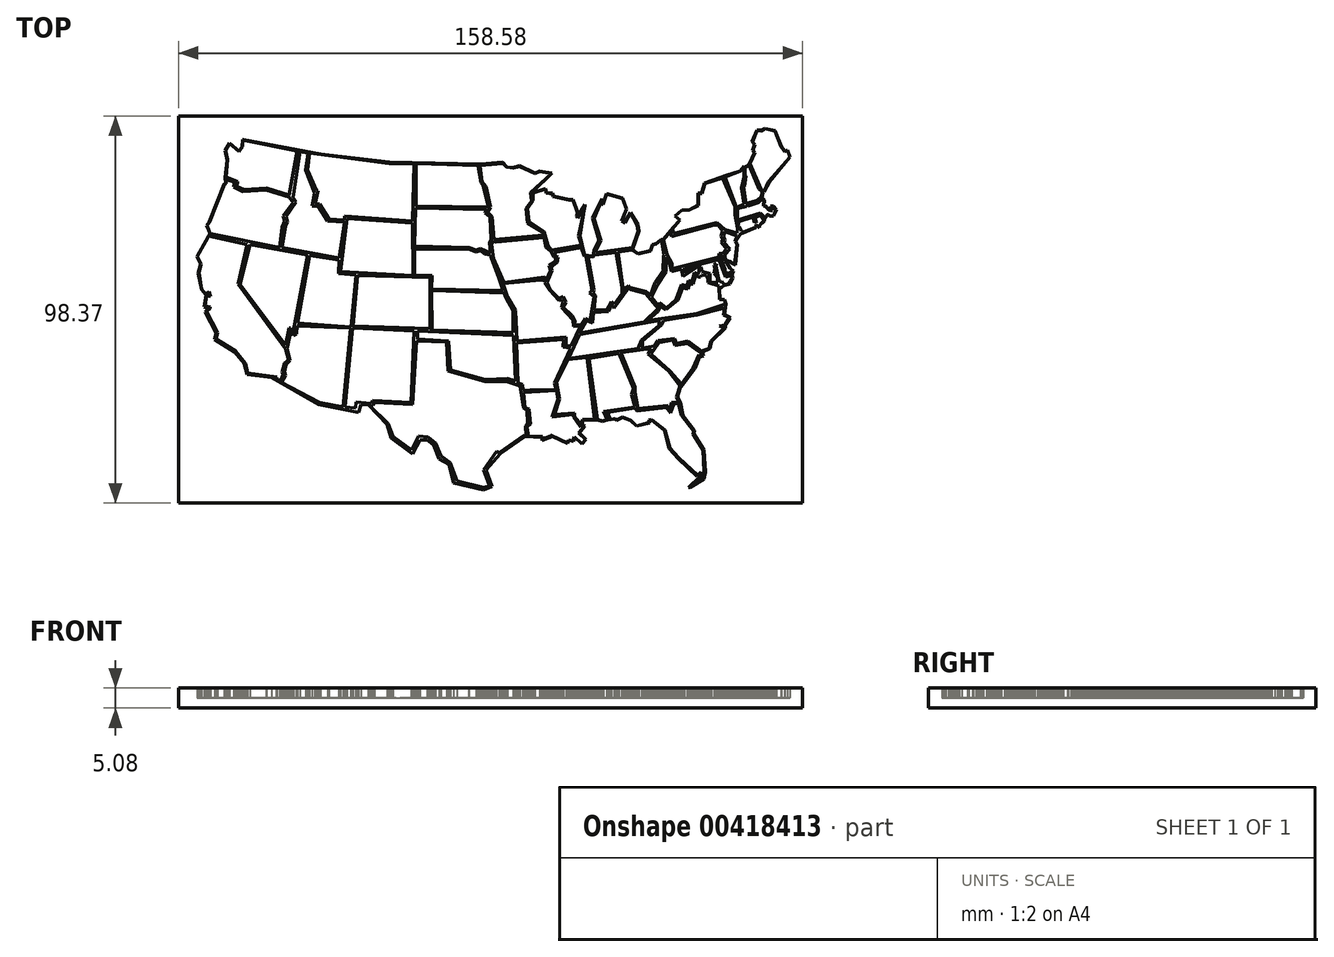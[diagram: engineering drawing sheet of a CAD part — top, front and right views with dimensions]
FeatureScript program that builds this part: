
annotation { "Feature Type Name" : "Feature", "Feature Type Description" : "" }
export const myFeature = defineFeature(function(context is Context, id is Id, definition is map)
    precondition{}
    {
        {
            var Q0;
            Q0=qCreatedBy(makeId("Top.planeOp"),FACE);
            var sketch = newSketch(context, id + "F0", { "sketchPlane" : qUnion([Q0])});
            skLineSegment(sketch, "E0", {"start": v(142.1, 83.2) * mm, "end": v(143.4, 85.93) * mm});
            skLineSegment(sketch, "E1", {"start": v(143.4, 85.93) * mm, "end": v(142.9, 86.54) * mm});
            skLineSegment(sketch, "E2", {"start": v(142.9, 86.54) * mm, "end": v(143.4, 87.95) * mm});
            skLineSegment(sketch, "E3", {"start": v(143.4, 87.95) * mm, "end": v(142.77, 88.66) * mm});
            skLineSegment(sketch, "E4", {"start": v(142.77, 88.66) * mm, "end": v(143.93, 91.52) * mm});
            skLineSegment(sketch, "E5", {"start": v(143.93, 91.52) * mm, "end": v(144.93, 91.37) * mm});
            skLineSegment(sketch, "E6", {"start": v(144.93, 91.37) * mm, "end": v(145.98, 92.05) * mm});
            skLineSegment(sketch, "E7", {"start": v(145.98, 92.05) * mm, "end": v(148.4, 91.43) * mm});
            skLineSegment(sketch, "E8", {"start": v(148.4, 91.43) * mm, "end": v(150, 87.44) * mm});
            skLineSegment(sketch, "E9", {"start": v(150, 87.44) * mm, "end": v(150.93, 86.26) * mm});
            skLineSegment(sketch, "E10", {"start": v(150.93, 86.26) * mm, "end": v(151.6, 86.54) * mm});
            skLineSegment(sketch, "E11", {"start": v(151.6, 86.54) * mm, "end": v(152.28, 84.86) * mm});
            skLineSegment(sketch, "E12", {"start": v(152.28, 84.86) * mm, "end": v(146.82, 78.58) * mm});
            skLineSegment(sketch, "E13", {"start": v(146.82, 78.58) * mm, "end": v(145.67, 76.04) * mm});
            skLineSegment(sketch, "E14", {"start": v(145.67, 76.04) * mm, "end": v(144.93, 76.69) * mm});
            skLineSegment(sketch, "E15", {"start": v(144.93, 76.69) * mm, "end": v(142.1, 83.2) * mm});
            skLineSegment(sketch, "E16", {"start": v(140.9, 82.01) * mm, "end": v(140.9, 80.38) * mm});
            skLineSegment(sketch, "E17", {"start": v(140.9, 80.38) * mm, "end": v(141.07, 79.99) * mm});
            skLineSegment(sketch, "E18", {"start": v(141.07, 79.99) * mm, "end": v(140.7, 77.26) * mm});
            skLineSegment(sketch, "E19", {"start": v(140.7, 77.26) * mm, "end": v(140.43, 76.96) * mm});
            skLineSegment(sketch, "E20", {"start": v(140.43, 76.96) * mm, "end": v(140.58, 76.6) * mm});
            skLineSegment(sketch, "E21", {"start": v(140.58, 76.6) * mm, "end": v(141.1, 72.95) * mm});
            skLineSegment(sketch, "E22", {"start": v(141.1, 72.95) * mm, "end": v(143.78, 73.74) * mm});
            skLineSegment(sketch, "E23", {"start": v(143.78, 73.74) * mm, "end": v(143.93, 73.74) * mm});
            skLineSegment(sketch, "E24", {"start": v(143.93, 73.74) * mm, "end": v(144.3, 74.17) * mm});
            skLineSegment(sketch, "E25", {"start": v(144.3, 74.17) * mm, "end": v(144.93, 74.63) * mm});
            skLineSegment(sketch, "E26", {"start": v(144.93, 74.63) * mm, "end": v(145.3, 75.9) * mm});
            skLineSegment(sketch, "E27", {"start": v(145.3, 75.9) * mm, "end": v(144.41, 76.69) * mm});
            skLineSegment(sketch, "E28", {"start": v(144.41, 76.69) * mm, "end": v(141.85, 82.82) * mm});
            skLineSegment(sketch, "E29", {"start": v(141.85, 82.82) * mm, "end": v(140.9, 82.01) * mm});
            skLineSegment(sketch, "E30", {"start": v(135.75, 79.78) * mm, "end": v(139.67, 81.2) * mm});
            skPoint(sketch, "E30.endSnap0", {"position": v(140.9, 81.2) * mm});
            skLineSegment(sketch, "E31", {"start": v(139.67, 81.2) * mm, "end": v(140.58, 82.24) * mm});
            skLineSegment(sketch, "E32", {"start": v(140.58, 82.24) * mm, "end": v(140.58, 79.7) * mm});
            skLineSegment(sketch, "E33", {"start": v(140.58, 79.7) * mm, "end": v(139.97, 76.96) * mm});
            skLineSegment(sketch, "E34", {"start": v(139.97, 76.96) * mm, "end": v(140.58, 72.84) * mm});
            skLineSegment(sketch, "E35", {"start": v(140.58, 72.84) * mm, "end": v(138.65, 72) * mm});
            skLineSegment(sketch, "E36", {"start": v(138.65, 72) * mm, "end": v(135.75, 79.78) * mm});
            skLineSegment(sketch, "E37", {"start": v(138.98, 71.76) * mm, "end": v(141.12, 72.27) * mm});
            skLineSegment(sketch, "E38", {"start": v(141.12, 72.27) * mm, "end": v(141.12, 72.54) * mm});
            skLineSegment(sketch, "E39", {"start": v(141.12, 72.54) * mm, "end": v(141.5, 72.54) * mm});
            skLineSegment(sketch, "E40", {"start": v(141.5, 72.54) * mm, "end": v(141.65, 72.42) * mm});
            skLineSegment(sketch, "E41", {"start": v(141.65, 72.42) * mm, "end": v(144.27, 73.3) * mm});
            skLineSegment(sketch, "E42", {"start": v(144.27, 73.3) * mm, "end": v(145.25, 74.16) * mm});
            skLineSegment(sketch, "E43", {"start": v(145.25, 74.16) * mm, "end": v(145.67, 73.8) * mm});
            skLineSegment(sketch, "E44", {"start": v(145.67, 73.8) * mm, "end": v(145.67, 73.18) * mm});
            skLineSegment(sketch, "E45", {"start": v(145.67, 73.18) * mm, "end": v(145.58, 73.08) * mm});
            skLineSegment(sketch, "E46", {"start": v(145.58, 73.08) * mm, "end": v(145.49, 72.42) * mm});
            skLineSegment(sketch, "E47", {"start": v(145.49, 72.42) * mm, "end": v(145.98, 72.42) * mm});
            skLineSegment(sketch, "E48", {"start": v(145.98, 72.42) * mm, "end": v(146.69, 71.66) * mm});
            skLineSegment(sketch, "E49", {"start": v(146.69, 71.66) * mm, "end": v(147.33, 71.25) * mm});
            skLineSegment(sketch, "E50", {"start": v(147.33, 71.25) * mm, "end": v(147.86, 71.25) * mm});
            skLineSegment(sketch, "E51", {"start": v(147.86, 71.25) * mm, "end": v(147.43, 72.3) * mm});
            skLineSegment(sketch, "E52", {"start": v(147.43, 72.3) * mm, "end": v(148.13, 72.3) * mm});
            skLineSegment(sketch, "E53", {"start": v(148.13, 72.3) * mm, "end": v(148.77, 71.52) * mm});
            skLineSegment(sketch, "E54", {"start": v(148.77, 71.52) * mm, "end": v(148.05, 69.86) * mm});
            skLineSegment(sketch, "E55", {"start": v(148.05, 69.86) * mm, "end": v(147.07, 69.86) * mm});
            skLineSegment(sketch, "E56", {"start": v(147.07, 69.86) * mm, "end": v(146.82, 70.26) * mm});
            skLineSegment(sketch, "E57", {"start": v(146.82, 70.26) * mm, "end": v(146.6, 70.26) * mm});
            skLineSegment(sketch, "E58", {"start": v(146.6, 70.26) * mm, "end": v(145.87, 69.41) * mm});
            skLineSegment(sketch, "E59", {"start": v(145.87, 69.41) * mm, "end": v(144.73, 70.58) * mm});
            skLineSegment(sketch, "E60", {"start": v(144.73, 70.58) * mm, "end": v(138.93, 68.75) * mm});
            skLineSegment(sketch, "E61", {"start": v(138.93, 68.75) * mm, "end": v(138.98, 71.76) * mm});
            skLineSegment(sketch, "E62", {"start": v(130.7, 78.1) * mm, "end": v(135.15, 79.5) * mm});
            skLineSegment(sketch, "E63", {"start": v(135.15, 79.5) * mm, "end": v(138.3, 72.26) * mm});
            skLineSegment(sketch, "E64", {"start": v(138.3, 72.26) * mm, "end": v(138.3, 70.26) * mm});
            skLineSegment(sketch, "E65", {"start": v(138.3, 70.26) * mm, "end": v(138.98, 66.73) * mm});
            skLineSegment(sketch, "E66", {"start": v(138.98, 66.73) * mm, "end": v(138.8, 65.53) * mm});
            skLineSegment(sketch, "E67", {"start": v(138.8, 65.53) * mm, "end": v(135.75, 66.39) * mm});
            skLineSegment(sketch, "E68", {"start": v(135.75, 66.39) * mm, "end": v(133.73, 68.15) * mm});
            skLineSegment(sketch, "E69", {"start": v(133.73, 68.15) * mm, "end": v(122.67, 65.38) * mm});
            skLineSegment(sketch, "E70", {"start": v(122.67, 65.38) * mm, "end": v(122.4, 66.5) * mm});
            skLineSegment(sketch, "E71", {"start": v(122.4, 66.5) * mm, "end": v(124.34, 68.75) * mm});
            skLineSegment(sketch, "E72", {"start": v(124.34, 68.75) * mm, "end": v(123.07, 69.86) * mm});
            skLineSegment(sketch, "E73", {"start": v(123.07, 69.86) * mm, "end": v(124.88, 71.3) * mm});
            skLineSegment(sketch, "E74", {"start": v(124.88, 71.3) * mm, "end": v(126.69, 71.3) * mm});
            skLineSegment(sketch, "E75", {"start": v(126.69, 71.3) * mm, "end": v(129.1, 72.54) * mm});
            skLineSegment(sketch, "E76", {"start": v(129.1, 72.54) * mm, "end": v(129.1, 75.55) * mm});
            skLineSegment(sketch, "E77", {"start": v(129.1, 75.55) * mm, "end": v(129.88, 75.55) * mm});
            skLineSegment(sketch, "E78", {"start": v(129.88, 75.55) * mm, "end": v(130.7, 78.1) * mm});
            skLineSegment(sketch, "E79", {"start": v(140.43, 65.77) * mm, "end": v(140.2, 65.96) * mm});
            skLineSegment(sketch, "E80", {"start": v(140.2, 65.96) * mm, "end": v(139.97, 65.96) * mm});
            skLineSegment(sketch, "E81", {"start": v(139.97, 65.96) * mm, "end": v(139.27, 67.11) * mm});
            skLineSegment(sketch, "E82", {"start": v(139.27, 67.11) * mm, "end": v(139.07, 67.55) * mm});
            skLineSegment(sketch, "E83", {"start": v(139.07, 67.55) * mm, "end": v(139.28, 68.46) * mm});
            skLineSegment(sketch, "E84", {"start": v(139.28, 68.46) * mm, "end": v(142.9, 69.55) * mm});
            skLineSegment(sketch, "E85", {"start": v(142.9, 69.55) * mm, "end": v(143.26, 68.12) * mm});
            skLineSegment(sketch, "E86", {"start": v(143.26, 68.12) * mm, "end": v(143.3, 68.46) * mm});
            skLineSegment(sketch, "E87", {"start": v(143.3, 68.46) * mm, "end": v(143.78, 68.05) * mm});
            skLineSegment(sketch, "E88", {"start": v(143.78, 68.05) * mm, "end": v(143.44, 69.41) * mm});
            skLineSegment(sketch, "E89", {"start": v(143.44, 69.41) * mm, "end": v(144.61, 69.93) * mm});
            skLineSegment(sketch, "E90", {"start": v(144.61, 69.93) * mm, "end": v(145.67, 68.75) * mm});
            skLineSegment(sketch, "E91", {"start": v(145.67, 68.75) * mm, "end": v(144.41, 67.3) * mm});
            skLineSegment(sketch, "E92", {"start": v(144.41, 67.3) * mm, "end": v(144.52, 66.9) * mm});
            skLineSegment(sketch, "E93", {"start": v(144.52, 66.9) * mm, "end": v(143.6, 67.7) * mm});
            skLineSegment(sketch, "E94", {"start": v(143.6, 67.7) * mm, "end": v(143.6, 67) * mm});
            skLineSegment(sketch, "E95", {"start": v(143.6, 67) * mm, "end": v(140.43, 65.77) * mm});
            skLineSegment(sketch, "E96", {"start": v(135.8, 65.86) * mm, "end": v(138.8, 64.74) * mm});
            skLineSegment(sketch, "E97", {"start": v(138.8, 64.74) * mm, "end": v(138.28, 63.36) * mm});
            skLineSegment(sketch, "E98", {"start": v(138.28, 63.36) * mm, "end": v(138.78, 62.73) * mm});
            skLineSegment(sketch, "E99", {"start": v(138.78, 62.73) * mm, "end": v(138.24, 57.48) * mm});
            skLineSegment(sketch, "E100", {"start": v(138.24, 57.48) * mm, "end": v(137.17, 58.27) * mm});
            skLineSegment(sketch, "E101", {"start": v(137.17, 58.27) * mm, "end": v(136.29, 58.55) * mm});
            skLineSegment(sketch, "E102", {"start": v(136.29, 58.55) * mm, "end": v(135.92, 58.9) * mm});
            skLineSegment(sketch, "E103", {"start": v(135.92, 58.9) * mm, "end": v(135.79, 59.28) * mm});
            skLineSegment(sketch, "E104", {"start": v(135.79, 59.28) * mm, "end": v(135.72, 60) * mm});
            skLineSegment(sketch, "E105", {"start": v(135.72, 60) * mm, "end": v(136.98, 61.49) * mm});
            skLineSegment(sketch, "E106", {"start": v(136.98, 61.49) * mm, "end": v(135.47, 63.1) * mm});
            skLineSegment(sketch, "E107", {"start": v(135.47, 63.1) * mm, "end": v(135.7, 63.8) * mm});
            skLineSegment(sketch, "E108", {"start": v(135.7, 63.8) * mm, "end": v(135.36, 64.79) * mm});
            skLineSegment(sketch, "E109", {"start": v(135.36, 64.79) * mm, "end": v(135.8, 65.86) * mm});
            skLineSegment(sketch, "E110", {"start": v(137.81, 55.84) * mm, "end": v(136.98, 56.56) * mm});
            skLineSegment(sketch, "E111", {"start": v(136.98, 56.56) * mm, "end": v(136.38, 57.51) * mm});
            skLineSegment(sketch, "E112", {"start": v(136.38, 57.51) * mm, "end": v(135.7, 58.35) * mm});
            skLineSegment(sketch, "E113", {"start": v(135.7, 58.35) * mm, "end": v(135.36, 59.59) * mm});
            skLineSegment(sketch, "E114", {"start": v(135.36, 59.59) * mm, "end": v(134.6, 59.59) * mm});
            skLineSegment(sketch, "E115", {"start": v(134.6, 59.59) * mm, "end": v(134.7, 58.89) * mm});
            skLineSegment(sketch, "E116", {"start": v(134.7, 58.89) * mm, "end": v(134.91, 58.47) * mm});
            skLineSegment(sketch, "E117", {"start": v(134.91, 58.47) * mm, "end": v(135.8, 56.41) * mm});
            skLineSegment(sketch, "E118", {"start": v(135.8, 56.41) * mm, "end": v(135.8, 55.88) * mm});
            skLineSegment(sketch, "E119", {"start": v(135.8, 55.88) * mm, "end": v(136.08, 55.76) * mm});
            skLineSegment(sketch, "E120", {"start": v(136.08, 55.76) * mm, "end": v(136.3, 55.04) * mm});
            skLineSegment(sketch, "E121", {"start": v(136.3, 55.04) * mm, "end": v(137.81, 55.84) * mm});
            skLineSegment(sketch, "E122", {"start": v(121.87, 65.86) * mm, "end": v(122.17, 64.61) * mm});
            skLineSegment(sketch, "E123", {"start": v(122.17, 64.61) * mm, "end": v(133.01, 67.53) * mm});
            skLineSegment(sketch, "E124", {"start": v(133.01, 67.53) * mm, "end": v(133.97, 67.53) * mm});
            skLineSegment(sketch, "E125", {"start": v(133.97, 67.53) * mm, "end": v(135.14, 66.07) * mm});
            skLineSegment(sketch, "E126", {"start": v(135.14, 66.07) * mm, "end": v(134.7, 64.79) * mm});
            skLineSegment(sketch, "E127", {"start": v(134.7, 64.79) * mm, "end": v(135.23, 63.8) * mm});
            skLineSegment(sketch, "E128", {"start": v(135.23, 63.8) * mm, "end": v(134.7, 63.18) * mm});
            skLineSegment(sketch, "E129", {"start": v(134.7, 63.18) * mm, "end": v(136.12, 61.42) * mm});
            skLineSegment(sketch, "E130", {"start": v(136.12, 61.42) * mm, "end": v(135.1, 60.25) * mm});
            skLineSegment(sketch, "E131", {"start": v(135.1, 60.25) * mm, "end": v(134.3, 60.25) * mm});
            skLineSegment(sketch, "E132", {"start": v(134.3, 60.25) * mm, "end": v(134.3, 59.4) * mm});
            skLineSegment(sketch, "E133", {"start": v(134.3, 59.4) * mm, "end": v(122.58, 56.43) * mm});
            skLineSegment(sketch, "E134", {"start": v(122.58, 56.43) * mm, "end": v(122.28, 56.9) * mm});
            skLineSegment(sketch, "E135", {"start": v(122.28, 56.9) * mm, "end": v(122.28, 57.71) * mm});
            skLineSegment(sketch, "E136", {"start": v(122.28, 57.71) * mm, "end": v(121.07, 59.99) * mm});
            skLineSegment(sketch, "E137", {"start": v(121.07, 59.99) * mm, "end": v(120.12, 63.8) * mm});
            skLineSegment(sketch, "E138", {"start": v(120.12, 63.8) * mm, "end": v(121.87, 65.86) * mm});
            skLineSegment(sketch, "E139", {"start": v(120.75, 55.76) * mm, "end": v(120.75, 59.4) * mm});
            skLineSegment(sketch, "E140", {"start": v(120.75, 59.4) * mm, "end": v(121.65, 57.71) * mm});
            skLineSegment(sketch, "E141", {"start": v(121.65, 57.71) * mm, "end": v(121.87, 56.8) * mm});
            skLineSegment(sketch, "E142", {"start": v(121.87, 56.8) * mm, "end": v(122.13, 55.76) * mm});
            skLineSegment(sketch, "E143", {"start": v(122.13, 55.76) * mm, "end": v(124.75, 56.42) * mm});
            skLineSegment(sketch, "E144", {"start": v(124.75, 56.42) * mm, "end": v(125.03, 54.42) * mm});
            skLineSegment(sketch, "E145", {"start": v(125.03, 54.42) * mm, "end": v(128.7, 56.9) * mm});
            skLineSegment(sketch, "E146", {"start": v(128.7, 56.9) * mm, "end": v(129.2, 56.47) * mm});
            skLineSegment(sketch, "E147", {"start": v(129.2, 56.47) * mm, "end": v(129.2, 55.42) * mm});
            skPoint(sketch, "E147.endSnap0", {"position": v(124.9, 55.42) * mm});
            skLineSegment(sketch, "E148", {"start": v(129.2, 55.42) * mm, "end": v(128.78, 55.14) * mm});
            skLineSegment(sketch, "E149", {"start": v(128.78, 55.14) * mm, "end": v(127.98, 55.5) * mm});
            skLineSegment(sketch, "E150", {"start": v(127.98, 55.5) * mm, "end": v(127.41, 53.2) * mm});
            skLineSegment(sketch, "E151", {"start": v(127.41, 53.2) * mm, "end": v(126.5, 53.43) * mm});
            skLineSegment(sketch, "E152", {"start": v(126.5, 53.43) * mm, "end": v(126.18, 52.08) * mm});
            skLineSegment(sketch, "E153", {"start": v(126.18, 52.08) * mm, "end": v(124.65, 52.45) * mm});
            skLineSegment(sketch, "E154", {"start": v(124.65, 52.45) * mm, "end": v(123.3, 48.58) * mm});
            skLineSegment(sketch, "E155", {"start": v(123.3, 48.58) * mm, "end": v(120.9, 46.52) * mm});
            skLineSegment(sketch, "E156", {"start": v(120.9, 46.52) * mm, "end": v(119.1, 47.85) * mm});
            skLineSegment(sketch, "E157", {"start": v(119.1, 47.85) * mm, "end": v(118.98, 46.85) * mm});
            skLineSegment(sketch, "E158", {"start": v(118.98, 46.85) * mm, "end": v(117.14, 49.24) * mm});
            skLineSegment(sketch, "E159", {"start": v(117.14, 49.24) * mm, "end": v(118.59, 52.4) * mm});
            skLineSegment(sketch, "E160", {"start": v(118.59, 52.4) * mm, "end": v(120.75, 55.76) * mm});
            skLineSegment(sketch, "E161", {"start": v(127.84, 56.9) * mm, "end": v(125.51, 55.33) * mm});
            skLineSegment(sketch, "E162", {"start": v(125.51, 55.33) * mm, "end": v(125.51, 56.61) * mm});
            skLineSegment(sketch, "E163", {"start": v(125.51, 56.61) * mm, "end": v(134.3, 58.84) * mm});
            skLineSegment(sketch, "E164", {"start": v(134.3, 58.84) * mm, "end": v(135.87, 54.34) * mm});
            skLineSegment(sketch, "E165", {"start": v(135.87, 54.34) * mm, "end": v(137.41, 54.73) * mm});
            skLineSegment(sketch, "E166", {"start": v(137.41, 54.73) * mm, "end": v(137.58, 54.1) * mm});
            skLineSegment(sketch, "E167", {"start": v(137.58, 54.1) * mm, "end": v(137.03, 53.27) * mm});
            skLineSegment(sketch, "E168", {"start": v(137.03, 53.27) * mm, "end": v(136.82, 52.67) * mm});
            skLineSegment(sketch, "E169", {"start": v(136.82, 52.67) * mm, "end": v(135.6, 52.36) * mm});
            skLineSegment(sketch, "E170", {"start": v(135.6, 52.36) * mm, "end": v(135.03, 53.2) * mm});
            skLineSegment(sketch, "E171", {"start": v(135.03, 53.2) * mm, "end": v(134.42, 53.12) * mm});
            skLineSegment(sketch, "E172", {"start": v(134.42, 53.12) * mm, "end": v(134.07, 53.91) * mm});
            skLineSegment(sketch, "E173", {"start": v(134.07, 53.91) * mm, "end": v(133.44, 57.1) * mm});
            skLineSegment(sketch, "E174", {"start": v(133.44, 57.1) * mm, "end": v(133.65, 57.7) * mm});
            skLineSegment(sketch, "E175", {"start": v(133.65, 57.7) * mm, "end": v(132.98, 57.4) * mm});
            skLineSegment(sketch, "E176", {"start": v(132.98, 57.4) * mm, "end": v(133.22, 56.47) * mm});
            skLineSegment(sketch, "E177", {"start": v(133.22, 56.47) * mm, "end": v(133.01, 55.16) * mm});
            skLineSegment(sketch, "E178", {"start": v(133.01, 55.16) * mm, "end": v(133.82, 54.22) * mm});
            skLineSegment(sketch, "E179", {"start": v(133.82, 54.22) * mm, "end": v(133.88, 53.47) * mm});
            skLineSegment(sketch, "E180", {"start": v(133.88, 53.47) * mm, "end": v(134.02, 52.92) * mm});
            skLineSegment(sketch, "E181", {"start": v(134.02, 52.92) * mm, "end": v(132.2, 53.1) * mm});
            skLineSegment(sketch, "E182", {"start": v(132.2, 53.1) * mm, "end": v(131.99, 53.42) * mm});
            skLineSegment(sketch, "E183", {"start": v(131.99, 53.42) * mm, "end": v(131.99, 55.24) * mm});
            skLineSegment(sketch, "E184", {"start": v(131.99, 55.24) * mm, "end": v(129.94, 55.76) * mm});
            skLineSegment(sketch, "E185", {"start": v(129.94, 55.76) * mm, "end": v(129.65, 56.9) * mm});
            skLineSegment(sketch, "E186", {"start": v(129.65, 56.9) * mm, "end": v(129.3, 57.02) * mm});
            skLineSegment(sketch, "E187", {"start": v(129.3, 57.02) * mm, "end": v(128.7, 57.23) * mm});
            skLineSegment(sketch, "E188", {"start": v(128.7, 57.23) * mm, "end": v(127.84, 56.9) * mm});
            skLineSegment(sketch, "E189", {"start": v(129.2, 54.36) * mm, "end": v(128.32, 54.67) * mm});
            skLineSegment(sketch, "E190", {"start": v(128.32, 54.67) * mm, "end": v(127.6, 52.6) * mm});
            skLineSegment(sketch, "E191", {"start": v(127.6, 52.6) * mm, "end": v(126.74, 52.6) * mm});
            skLineSegment(sketch, "E192", {"start": v(126.74, 52.6) * mm, "end": v(126.42, 51.23) * mm});
            skLineSegment(sketch, "E193", {"start": v(126.42, 51.23) * mm, "end": v(125, 51.56) * mm});
            skLineSegment(sketch, "E194", {"start": v(125, 51.56) * mm, "end": v(123.89, 48.43) * mm});
            skLineSegment(sketch, "E195", {"start": v(123.89, 48.43) * mm, "end": v(120.75, 46.02) * mm});
            skLineSegment(sketch, "E196", {"start": v(120.75, 46.02) * mm, "end": v(119.34, 46.92) * mm});
            skLineSegment(sketch, "E197", {"start": v(119.34, 46.92) * mm, "end": v(118.75, 45.6) * mm});
            skLineSegment(sketch, "E198", {"start": v(118.75, 45.6) * mm, "end": v(116.14, 43.23) * mm});
            skLineSegment(sketch, "E199", {"start": v(116.14, 43.23) * mm, "end": v(128.7, 45) * mm});
            skLineSegment(sketch, "E200", {"start": v(128.7, 45) * mm, "end": v(135.87, 47.48) * mm});
            skLineSegment(sketch, "E201", {"start": v(135.87, 47.48) * mm, "end": v(135.6, 48.53) * mm});
            skLineSegment(sketch, "E202", {"start": v(135.6, 48.53) * mm, "end": v(134.42, 48.68) * mm});
            skLineSegment(sketch, "E203", {"start": v(134.42, 48.68) * mm, "end": v(134.3, 52.04) * mm});
            skLineSegment(sketch, "E204", {"start": v(134.3, 52.04) * mm, "end": v(131.47, 52.92) * mm});
            skLineSegment(sketch, "E205", {"start": v(131.47, 52.92) * mm, "end": v(131.47, 54.1) * mm});
            skLineSegment(sketch, "E206", {"start": v(131.47, 54.1) * mm, "end": v(131, 54.7) * mm});
            skLineSegment(sketch, "E207", {"start": v(131, 54.7) * mm, "end": v(129.8, 54.85) * mm});
            skLineSegment(sketch, "E208", {"start": v(129.8, 54.85) * mm, "end": v(129.5, 54.36) * mm});
            skLineSegment(sketch, "E209", {"start": v(129.5, 54.36) * mm, "end": v(129.2, 54.36) * mm});
            skLineSegment(sketch, "E210", {"start": v(116.82, 49.78) * mm, "end": v(118.03, 52.92) * mm});
            skLineSegment(sketch, "E211", {"start": v(118.03, 52.92) * mm, "end": v(119.86, 55.76) * mm});
            skLineSegment(sketch, "E212", {"start": v(119.86, 55.76) * mm, "end": v(120.3, 55.9) * mm});
            skLineSegment(sketch, "E213", {"start": v(120.3, 55.9) * mm, "end": v(120.03, 56.25) * mm});
            skLineSegment(sketch, "E214", {"start": v(120.03, 56.25) * mm, "end": v(120.12, 59.4) * mm});
            skLineSegment(sketch, "E215", {"start": v(120.12, 59.4) * mm, "end": v(120.32, 59.99) * mm});
            skLineSegment(sketch, "E216", {"start": v(120.32, 59.99) * mm, "end": v(119.59, 63.8) * mm});
            skLineSegment(sketch, "E217", {"start": v(119.59, 63.8) * mm, "end": v(118.25, 62.76) * mm});
            skLineSegment(sketch, "E218", {"start": v(118.25, 62.76) * mm, "end": v(117.42, 62.47) * mm});
            skLineSegment(sketch, "E219", {"start": v(117.42, 62.47) * mm, "end": v(116.87, 60.92) * mm});
            skLineSegment(sketch, "E220", {"start": v(116.87, 60.92) * mm, "end": v(113.69, 60.12) * mm});
            skLineSegment(sketch, "E221", {"start": v(113.69, 60.12) * mm, "end": v(112.1, 61.14) * mm});
            skLineSegment(sketch, "E222", {"start": v(112.1, 61.14) * mm, "end": v(108.59, 60.65) * mm});
            skLineSegment(sketch, "E223", {"start": v(108.59, 60.65) * mm, "end": v(109.99, 50.75) * mm});
            skLineSegment(sketch, "E224", {"start": v(109.99, 50.75) * mm, "end": v(110.61, 51.73) * mm});
            skLineSegment(sketch, "E225", {"start": v(110.61, 51.73) * mm, "end": v(111.24, 52.15) * mm});
            skLineSegment(sketch, "E226", {"start": v(111.24, 52.15) * mm, "end": v(111.65, 51.62) * mm});
            skLineSegment(sketch, "E227", {"start": v(111.65, 51.62) * mm, "end": v(115.72, 50.6) * mm});
            skLineSegment(sketch, "E228", {"start": v(115.72, 50.6) * mm, "end": v(116.82, 49.78) * mm});
            skLineSegment(sketch, "E229", {"start": v(111.35, 51.62) * mm, "end": v(111.74, 51.11) * mm});
            skPoint(sketch, "E229.endSnap0", {"position": v(113.69, 51.11) * mm});
            skLineSegment(sketch, "E230", {"start": v(111.74, 51.11) * mm, "end": v(115.63, 50.15) * mm});
            skLineSegment(sketch, "E231", {"start": v(115.63, 50.15) * mm, "end": v(116.82, 48.68) * mm});
            skLineSegment(sketch, "E232", {"start": v(116.82, 48.68) * mm, "end": v(118.75, 46.33) * mm});
            skLineSegment(sketch, "E233", {"start": v(118.75, 46.33) * mm, "end": v(115.21, 42.94) * mm});
            skLineSegment(sketch, "E234", {"start": v(115.21, 42.94) * mm, "end": v(98.8, 40.07) * mm});
            skLineSegment(sketch, "E235", {"start": v(98.8, 40.07) * mm, "end": v(100.55, 43.23) * mm});
            skLineSegment(sketch, "E236", {"start": v(100.55, 43.23) * mm, "end": v(102.06, 42.7) * mm});
            skLineSegment(sketch, "E237", {"start": v(102.06, 42.7) * mm, "end": v(102.38, 45.27) * mm});
            skLineSegment(sketch, "E238", {"start": v(102.38, 45.27) * mm, "end": v(106.2, 45.6) * mm});
            skLineSegment(sketch, "E239", {"start": v(106.2, 45.6) * mm, "end": v(106.99, 47.33) * mm});
            skLineSegment(sketch, "E240", {"start": v(106.99, 47.33) * mm, "end": v(107.61, 46.52) * mm});
            skLineSegment(sketch, "E241", {"start": v(107.61, 46.52) * mm, "end": v(111.35, 51.62) * mm});
            skLineSegment(sketch, "E242", {"start": v(98.8, 39.72) * mm, "end": v(118.98, 43.25) * mm});
            skLineSegment(sketch, "E243", {"start": v(118.98, 43.25) * mm, "end": v(118.98, 42.03) * mm});
            skLineSegment(sketch, "E244", {"start": v(118.98, 42.03) * mm, "end": v(114.59, 38.28) * mm});
            skLineSegment(sketch, "E245", {"start": v(114.59, 38.28) * mm, "end": v(113.73, 36.18) * mm});
            skLineSegment(sketch, "E246", {"start": v(113.73, 36.18) * mm, "end": v(95.99, 33.68) * mm});
            skLineSegment(sketch, "E247", {"start": v(95.99, 33.68) * mm, "end": v(98.8, 39.72) * mm});
            skLineSegment(sketch, "E248", {"start": v(120.12, 43.23) * mm, "end": v(128.7, 44.73) * mm});
            skLineSegment(sketch, "E249", {"start": v(128.7, 44.73) * mm, "end": v(135.6, 46.48) * mm});
            skLineSegment(sketch, "E250", {"start": v(135.6, 46.48) * mm, "end": v(135.44, 44.64) * mm});
            skLineSegment(sketch, "E251", {"start": v(135.44, 44.64) * mm, "end": v(136.9, 44) * mm});
            skLineSegment(sketch, "E252", {"start": v(136.9, 44) * mm, "end": v(135.7, 42.14) * mm});
            skLineSegment(sketch, "E253", {"start": v(135.7, 42.14) * mm, "end": v(134.42, 41.9) * mm});
            skLineSegment(sketch, "E254", {"start": v(134.42, 41.9) * mm, "end": v(135.6, 41.52) * mm});
            skLineSegment(sketch, "E255", {"start": v(135.6, 41.52) * mm, "end": v(132.2, 38.01) * mm});
            skLineSegment(sketch, "E256", {"start": v(132.2, 38.01) * mm, "end": v(131.75, 36.18) * mm});
            skLineSegment(sketch, "E257", {"start": v(131.75, 36.18) * mm, "end": v(129.85, 35.52) * mm});
            skLineSegment(sketch, "E258", {"start": v(129.85, 35.52) * mm, "end": v(126.36, 38.01) * mm});
            skLineSegment(sketch, "E259", {"start": v(126.36, 38.01) * mm, "end": v(123.43, 37.5) * mm});
            skLineSegment(sketch, "E260", {"start": v(123.43, 37.5) * mm, "end": v(122.9, 38.71) * mm});
            skLineSegment(sketch, "E261", {"start": v(122.9, 38.71) * mm, "end": v(118.75, 38.26) * mm});
            skLineSegment(sketch, "E262", {"start": v(118.75, 38.26) * mm, "end": v(117.84, 36.84) * mm});
            skLineSegment(sketch, "E263", {"start": v(117.84, 36.84) * mm, "end": v(114.8, 36.31) * mm});
            skLineSegment(sketch, "E264", {"start": v(114.8, 36.31) * mm, "end": v(114.8, 38.01) * mm});
            skLineSegment(sketch, "E265", {"start": v(114.8, 38.01) * mm, "end": v(119.6, 42.15) * mm});
            skLineSegment(sketch, "E266", {"start": v(119.6, 42.15) * mm, "end": v(120.12, 43.23) * mm});
            skLineSegment(sketch, "E267", {"start": v(107.66, 47.54) * mm, "end": v(109.61, 50.2) * mm});
            skLineSegment(sketch, "E268", {"start": v(109.61, 50.2) * mm, "end": v(109.61, 51.84) * mm});
            skLineSegment(sketch, "E269", {"start": v(109.61, 51.84) * mm, "end": v(108.1, 60.58) * mm});
            skLineSegment(sketch, "E270", {"start": v(108.1, 60.58) * mm, "end": v(102.65, 59.9) * mm});
            skLineSegment(sketch, "E271", {"start": v(102.65, 59.9) * mm, "end": v(102.25, 59.35) * mm});
            skLineSegment(sketch, "E272", {"start": v(102.25, 59.35) * mm, "end": v(100.9, 59.58) * mm});
            skLineSegment(sketch, "E273", {"start": v(100.9, 59.58) * mm, "end": v(102.44, 51.1) * mm});
            skLineSegment(sketch, "E274", {"start": v(102.44, 51.1) * mm, "end": v(102.2, 50.38) * mm});
            skLineSegment(sketch, "E275", {"start": v(102.2, 50.38) * mm, "end": v(102.91, 49.61) * mm});
            skLineSegment(sketch, "E276", {"start": v(102.91, 49.61) * mm, "end": v(102.44, 45.9) * mm});
            skLineSegment(sketch, "E277", {"start": v(102.44, 45.9) * mm, "end": v(105.84, 46.05) * mm});
            skLineSegment(sketch, "E278", {"start": v(105.84, 46.05) * mm, "end": v(106.99, 48.06) * mm});
            skLineSegment(sketch, "E279", {"start": v(106.99, 48.06) * mm, "end": v(107.66, 47.54) * mm});
            skLineSegment(sketch, "E280", {"start": v(124.68, 27.1) * mm, "end": v(127.7, 31.22) * mm});
            skLineSegment(sketch, "E281", {"start": v(127.7, 31.22) * mm, "end": v(129.22, 34.59) * mm});
            skLineSegment(sketch, "E282", {"start": v(129.22, 34.59) * mm, "end": v(129.83, 34.31) * mm});
            skLineSegment(sketch, "E283", {"start": v(129.83, 34.31) * mm, "end": v(129.66, 35.02) * mm});
            skLineSegment(sketch, "E284", {"start": v(129.66, 35.02) * mm, "end": v(126.26, 37.5) * mm});
            skLineSegment(sketch, "E285", {"start": v(126.26, 37.5) * mm, "end": v(123.1, 36.95) * mm});
            skLineSegment(sketch, "E286", {"start": v(123.1, 36.95) * mm, "end": v(122.53, 38.32) * mm});
            skLineSegment(sketch, "E287", {"start": v(122.53, 38.32) * mm, "end": v(119, 37.66) * mm});
            skLineSegment(sketch, "E288", {"start": v(119, 37.66) * mm, "end": v(116.91, 34.8) * mm});
            skLineSegment(sketch, "E289", {"start": v(116.91, 34.8) * mm, "end": v(121.76, 30.43) * mm});
            skLineSegment(sketch, "E290", {"start": v(121.76, 30.43) * mm, "end": v(124.68, 27.1) * mm});
            skLineSegment(sketch, "E291", {"start": v(116.91, 36.18) * mm, "end": v(109.61, 35.15) * mm});
            skLineSegment(sketch, "E292", {"start": v(109.61, 35.15) * mm, "end": v(109.46, 34.8) * mm});
            skLineSegment(sketch, "E293", {"start": v(109.46, 34.8) * mm, "end": v(112.92, 26.35) * mm});
            skLineSegment(sketch, "E294", {"start": v(112.92, 26.35) * mm, "end": v(112.92, 24.99) * mm});
            skLineSegment(sketch, "E295", {"start": v(112.92, 24.99) * mm, "end": v(113.73, 20.9) * mm});
            skLineSegment(sketch, "E296", {"start": v(113.73, 20.9) * mm, "end": v(121.26, 21.7) * mm});
            skLineSegment(sketch, "E297", {"start": v(121.26, 21.7) * mm, "end": v(121.76, 20.72) * mm});
            skLineSegment(sketch, "E298", {"start": v(121.76, 20.72) * mm, "end": v(122.17, 22.47) * mm});
            skLineSegment(sketch, "E299", {"start": v(122.17, 22.47) * mm, "end": v(124.13, 22.47) * mm});
            skLineSegment(sketch, "E300", {"start": v(124.13, 22.47) * mm, "end": v(123.43, 23.82) * mm});
            skLineSegment(sketch, "E301", {"start": v(123.43, 23.82) * mm, "end": v(124.3, 26.69) * mm});
            skLineSegment(sketch, "E302", {"start": v(124.3, 26.69) * mm, "end": v(121.42, 30.43) * mm});
            skLineSegment(sketch, "E303", {"start": v(121.42, 30.43) * mm, "end": v(116.23, 34.8) * mm});
            skLineSegment(sketch, "E304", {"start": v(116.23, 34.8) * mm, "end": v(116.91, 36.18) * mm});
            skLineSegment(sketch, "E305", {"start": v(101.2, 33.68) * mm, "end": v(103.4, 18.14) * mm});
            skLineSegment(sketch, "E306", {"start": v(103.4, 18.14) * mm, "end": v(104.61, 17.72) * mm});
            skLineSegment(sketch, "E307", {"start": v(104.61, 17.72) * mm, "end": v(105.77, 18.2) * mm});
            skLineSegment(sketch, "E308", {"start": v(105.77, 18.2) * mm, "end": v(104.95, 20.21) * mm});
            skLineSegment(sketch, "E309", {"start": v(104.95, 20.21) * mm, "end": v(112.86, 21.33) * mm});
            skLineSegment(sketch, "E310", {"start": v(112.86, 21.33) * mm, "end": v(112.05, 24.54) * mm});
            skLineSegment(sketch, "E311", {"start": v(112.05, 24.54) * mm, "end": v(112.47, 26.07) * mm});
            skLineSegment(sketch, "E312", {"start": v(112.47, 26.07) * mm, "end": v(108.83, 34.94) * mm});
            skLineSegment(sketch, "E313", {"start": v(108.83, 34.94) * mm, "end": v(101.2, 33.68) * mm});
            skLineSegment(sketch, "E314", {"start": v(106.87, 18.2) * mm, "end": v(106.42, 18.6) * mm});
            skLineSegment(sketch, "E315", {"start": v(106.42, 18.6) * mm, "end": v(105.88, 19.9) * mm});
            skLineSegment(sketch, "E316", {"start": v(105.88, 19.9) * mm, "end": v(112.92, 21.02) * mm});
            skLineSegment(sketch, "E317", {"start": v(112.92, 21.02) * mm, "end": v(113.38, 20.24) * mm});
            skLineSegment(sketch, "E318", {"start": v(113.38, 20.24) * mm, "end": v(120.86, 21.22) * mm});
            skPoint(sketch, "E318.endSnap0", {"position": v(121.51, 21.22) * mm});
            skLineSegment(sketch, "E319", {"start": v(120.86, 21.22) * mm, "end": v(121.94, 19.82) * mm});
            skLineSegment(sketch, "E320", {"start": v(121.94, 19.82) * mm, "end": v(122.8, 22.16) * mm});
            skLineSegment(sketch, "E321", {"start": v(122.8, 22.16) * mm, "end": v(123.97, 22.04) * mm});
            skLineSegment(sketch, "E322", {"start": v(123.97, 22.04) * mm, "end": v(124.72, 19.1) * mm});
            skLineSegment(sketch, "E323", {"start": v(124.72, 19.1) * mm, "end": v(127.76, 15.24) * mm});
            skLineSegment(sketch, "E324", {"start": v(127.76, 15.24) * mm, "end": v(127.61, 14.46) * mm});
            skLineSegment(sketch, "E325", {"start": v(127.61, 14.46) * mm, "end": v(130.15, 10.34) * mm});
            skLineSegment(sketch, "E326", {"start": v(130.15, 10.34) * mm, "end": v(130.4, 4.8) * mm});
            skLineSegment(sketch, "E327", {"start": v(130.4, 4.8) * mm, "end": v(130.03, 3.17) * mm});
            skLineSegment(sketch, "E328", {"start": v(130.03, 3.17) * mm, "end": v(127, 1.13) * mm});
            skLineSegment(sketch, "E329", {"start": v(127, 1.13) * mm, "end": v(129.65, 3.64) * mm});
            skLineSegment(sketch, "E330", {"start": v(129.65, 3.64) * mm, "end": v(129.65, 4.74) * mm});
            skLineSegment(sketch, "E331", {"start": v(129.65, 4.74) * mm, "end": v(128.75, 4.02) * mm});
            skLineSegment(sketch, "E332", {"start": v(128.75, 4.02) * mm, "end": v(124.13, 8.32) * mm});
            skLineSegment(sketch, "E333", {"start": v(124.13, 8.32) * mm, "end": v(121.84, 10.87) * mm});
            skLineSegment(sketch, "E334", {"start": v(121.84, 10.87) * mm, "end": v(120.6, 15.44) * mm});
            skLineSegment(sketch, "E335", {"start": v(120.6, 15.44) * mm, "end": v(117.12, 18.2) * mm});
            skLineSegment(sketch, "E336", {"start": v(117.12, 18.2) * mm, "end": v(116.5, 18.02) * mm});
            skLineSegment(sketch, "E337", {"start": v(116.5, 18.02) * mm, "end": v(116.5, 17.34) * mm});
            skLineSegment(sketch, "E338", {"start": v(116.5, 17.34) * mm, "end": v(113.3, 16.54) * mm});
            skLineSegment(sketch, "E339", {"start": v(113.3, 16.54) * mm, "end": v(111.86, 17.9) * mm});
            skLineSegment(sketch, "E340", {"start": v(111.86, 17.9) * mm, "end": v(109.73, 18.78) * mm});
            skLineSegment(sketch, "E341", {"start": v(109.73, 18.78) * mm, "end": v(108.17, 18.05) * mm});
            skLineSegment(sketch, "E342", {"start": v(108.17, 18.05) * mm, "end": v(107.82, 18.39) * mm});
            skLineSegment(sketch, "E343", {"start": v(102.65, 18.14) * mm, "end": v(99.56, 18.14) * mm});
            skLineSegment(sketch, "E344", {"start": v(99.56, 18.14) * mm, "end": v(99.3, 16.78) * mm});
            skLineSegment(sketch, "E345", {"start": v(99.3, 16.78) * mm, "end": v(97.57, 18.94) * mm});
            skLineSegment(sketch, "E346", {"start": v(97.57, 18.94) * mm, "end": v(97.57, 19.8) * mm});
            skLineSegment(sketch, "E347", {"start": v(97.57, 19.8) * mm, "end": v(92.5, 19.35) * mm});
            skLineSegment(sketch, "E348", {"start": v(92.5, 19.35) * mm, "end": v(93.69, 23.33) * mm});
            skLineSegment(sketch, "E349", {"start": v(93.69, 23.33) * mm, "end": v(92.93, 27.54) * mm});
            skLineSegment(sketch, "E350", {"start": v(92.93, 27.54) * mm, "end": v(95.87, 33.43) * mm});
            skLineSegment(sketch, "E351", {"start": v(95.87, 33.43) * mm, "end": v(100.67, 33.86) * mm});
            skLineSegment(sketch, "E352", {"start": v(100.67, 33.86) * mm, "end": v(102.65, 18.14) * mm});
            skLineSegment(sketch, "E353", {"start": v(99.45, 12.1) * mm, "end": v(100.36, 13.06) * mm});
            skLineSegment(sketch, "E354", {"start": v(100.36, 13.06) * mm, "end": v(98.61, 14.72) * mm});
            skLineSegment(sketch, "E355", {"start": v(98.61, 14.72) * mm, "end": v(99.96, 16.42) * mm});
            skLineSegment(sketch, "E356", {"start": v(99.96, 16.42) * mm, "end": v(99.5, 16.43) * mm});
            skLineSegment(sketch, "E357", {"start": v(99.5, 16.43) * mm, "end": v(99.07, 16.23) * mm});
            skLineSegment(sketch, "E358", {"start": v(99.07, 16.23) * mm, "end": v(97.24, 18.72) * mm});
            skLineSegment(sketch, "E359", {"start": v(97.24, 18.72) * mm, "end": v(97.24, 19.43) * mm});
            skLineSegment(sketch, "E360", {"start": v(97.24, 19.43) * mm, "end": v(91.88, 18.76) * mm});
            skLineSegment(sketch, "E361", {"start": v(91.88, 18.76) * mm, "end": v(93.32, 23.33) * mm});
            skLineSegment(sketch, "E362", {"start": v(93.32, 23.33) * mm, "end": v(92.92, 25.53) * mm});
            skLineSegment(sketch, "E363", {"start": v(92.92, 25.53) * mm, "end": v(84.63, 25.03) * mm});
            skLineSegment(sketch, "E364", {"start": v(84.63, 25.03) * mm, "end": v(84.98, 21.1) * mm});
            skLineSegment(sketch, "E365", {"start": v(84.98, 21.1) * mm, "end": v(86.01, 20.8) * mm});
            skLineSegment(sketch, "E366", {"start": v(86.01, 20.8) * mm, "end": v(86.36, 16.97) * mm});
            skLineSegment(sketch, "E367", {"start": v(86.36, 16.97) * mm, "end": v(85.48, 16.23) * mm});
            skLineSegment(sketch, "E368", {"start": v(85.48, 16.23) * mm, "end": v(85.84, 13.84) * mm});
            skLineSegment(sketch, "E369", {"start": v(85.84, 13.84) * mm, "end": v(89.46, 13.79) * mm});
            skLineSegment(sketch, "E370", {"start": v(89.46, 13.79) * mm, "end": v(89.47, 13.14) * mm});
            skLineSegment(sketch, "E371", {"start": v(89.47, 13.14) * mm, "end": v(91.4, 13.9) * mm});
            skLineSegment(sketch, "E372", {"start": v(91.4, 13.9) * mm, "end": v(91.43, 14.2) * mm});
            skLineSegment(sketch, "E373", {"start": v(91.43, 14.2) * mm, "end": v(95.74, 12.2) * mm});
            skLineSegment(sketch, "E374", {"start": v(95.74, 12.2) * mm, "end": v(95.99, 12.96) * mm});
            skLineSegment(sketch, "E375", {"start": v(95.99, 12.96) * mm, "end": v(97.2, 12.69) * mm});
            skLineSegment(sketch, "E376", {"start": v(97.2, 12.69) * mm, "end": v(97.44, 13.74) * mm});
            skLineSegment(sketch, "E377", {"start": v(97.44, 13.74) * mm, "end": v(99.45, 12.1) * mm});
            skLineSegment(sketch, "E378", {"start": v(96.52, 36.22) * mm, "end": v(92.5, 27.44) * mm});
            skLineSegment(sketch, "E379", {"start": v(92.5, 27.44) * mm, "end": v(92.8, 25.8) * mm});
            skLineSegment(sketch, "E380", {"start": v(92.8, 25.8) * mm, "end": v(86.3, 25.67) * mm});
            skLineSegment(sketch, "E381", {"start": v(86.3, 25.67) * mm, "end": v(86.09, 25.55) * mm});
            skLineSegment(sketch, "E382", {"start": v(86.09, 25.55) * mm, "end": v(84.47, 25.57) * mm});
            skLineSegment(sketch, "E383", {"start": v(84.47, 25.57) * mm, "end": v(84.37, 27.03) * mm});
            skLineSegment(sketch, "E384", {"start": v(84.37, 27.03) * mm, "end": v(83.17, 27.37) * mm});
            skLineSegment(sketch, "E385", {"start": v(83.17, 27.37) * mm, "end": v(82.78, 37.54) * mm});
            skLineSegment(sketch, "E386", {"start": v(82.78, 37.54) * mm, "end": v(94.71, 38.4) * mm});
            skLineSegment(sketch, "E387", {"start": v(94.71, 38.4) * mm, "end": v(94.61, 36.56) * mm});
            skLineSegment(sketch, "E388", {"start": v(94.61, 36.56) * mm, "end": v(96.31, 36.33) * mm});
            skLineSegment(sketch, "E389", {"start": v(96.31, 36.33) * mm, "end": v(96.52, 36.22) * mm});
            skLineSegment(sketch, "E390", {"start": v(99.34, 42.09) * mm, "end": v(100.32, 43.84) * mm});
            skLineSegment(sketch, "E391", {"start": v(100.32, 43.84) * mm, "end": v(101.48, 43.2) * mm});
            skLineSegment(sketch, "E392", {"start": v(101.48, 43.2) * mm, "end": v(102.52, 49.35) * mm});
            skLineSegment(sketch, "E393", {"start": v(102.52, 49.35) * mm, "end": v(101.39, 50.3) * mm});
            skLineSegment(sketch, "E394", {"start": v(101.39, 50.3) * mm, "end": v(101.98, 51) * mm});
            skLineSegment(sketch, "E395", {"start": v(101.98, 51) * mm, "end": v(100.42, 59.58) * mm});
            skLineSegment(sketch, "E396", {"start": v(100.42, 59.58) * mm, "end": v(100.05, 59.59) * mm});
            skLineSegment(sketch, "E397", {"start": v(100.05, 59.59) * mm, "end": v(99.24, 61.77) * mm});
            skLineSegment(sketch, "E398", {"start": v(99.24, 61.77) * mm, "end": v(92.27, 60.51) * mm});
            skLineSegment(sketch, "E399", {"start": v(92.27, 60.51) * mm, "end": v(92.86, 59.58) * mm});
            skLineSegment(sketch, "E400", {"start": v(92.86, 59.58) * mm, "end": v(93.4, 59.35) * mm});
            skLineSegment(sketch, "E401", {"start": v(93.4, 59.35) * mm, "end": v(93.08, 57.97) * mm});
            skLineSegment(sketch, "E402", {"start": v(93.08, 57.97) * mm, "end": v(91.61, 56.91) * mm});
            skLineSegment(sketch, "E403", {"start": v(91.61, 56.91) * mm, "end": v(91.87, 55.94) * mm});
            skLineSegment(sketch, "E404", {"start": v(91.87, 55.94) * mm, "end": v(90.57, 52.9) * mm});
            skLineSegment(sketch, "E405", {"start": v(90.57, 52.9) * mm, "end": v(91.35, 51.11) * mm});
            skLineSegment(sketch, "E406", {"start": v(91.35, 51.11) * mm, "end": v(93.6, 48.94) * mm});
            skLineSegment(sketch, "E407", {"start": v(93.6, 48.94) * mm, "end": v(94.6, 49.44) * mm});
            skLineSegment(sketch, "E408", {"start": v(94.6, 49.44) * mm, "end": v(95.34, 47.96) * mm});
            skLineSegment(sketch, "E409", {"start": v(95.34, 47.96) * mm, "end": v(94.65, 46.7) * mm});
            skLineSegment(sketch, "E410", {"start": v(94.65, 46.7) * mm, "end": v(96.91, 44.51) * mm});
            skLineSegment(sketch, "E411", {"start": v(96.91, 44.51) * mm, "end": v(97.62, 43.13) * mm});
            skLineSegment(sketch, "E412", {"start": v(97.62, 43.13) * mm, "end": v(97.59, 42.18) * mm});
            skLineSegment(sketch, "E413", {"start": v(97.59, 42.18) * mm, "end": v(99.34, 42.09) * mm});
            skLineSegment(sketch, "E414", {"start": v(112.28, 61.84) * mm, "end": v(113.72, 65.86) * mm});
            skLineSegment(sketch, "E415", {"start": v(113.72, 65.86) * mm, "end": v(113.41, 67.55) * mm});
            skLineSegment(sketch, "E416", {"start": v(113.41, 67.55) * mm, "end": v(111.74, 70.57) * mm});
            skLineSegment(sketch, "E417", {"start": v(111.74, 70.57) * mm, "end": v(110.34, 68.06) * mm});
            skLineSegment(sketch, "E418", {"start": v(110.34, 68.06) * mm, "end": v(109.42, 68.58) * mm});
            skLineSegment(sketch, "E419", {"start": v(109.42, 68.58) * mm, "end": v(110.71, 71.65) * mm});
            skLineSegment(sketch, "E420", {"start": v(110.71, 71.65) * mm, "end": v(109.75, 74.3) * mm});
            skLineSegment(sketch, "E421", {"start": v(109.75, 74.3) * mm, "end": v(105.66, 75.44) * mm});
            skLineSegment(sketch, "E422", {"start": v(105.66, 75.44) * mm, "end": v(104.82, 72.73) * mm});
            skLineSegment(sketch, "E423", {"start": v(104.82, 72.73) * mm, "end": v(104.4, 72.85) * mm});
            skLineSegment(sketch, "E424", {"start": v(104.4, 72.85) * mm, "end": v(104.51, 74) * mm});
            skLineSegment(sketch, "E425", {"start": v(104.51, 74) * mm, "end": v(102.47, 69.18) * mm});
            skLineSegment(sketch, "E426", {"start": v(102.47, 69.18) * mm, "end": v(104.27, 63.65) * mm});
            skLineSegment(sketch, "E427", {"start": v(104.27, 63.65) * mm, "end": v(102.83, 61) * mm});
            skLineSegment(sketch, "E428", {"start": v(102.83, 61) * mm, "end": v(103, 60.52) * mm});
            skLineSegment(sketch, "E429", {"start": v(103, 60.52) * mm, "end": v(112.28, 61.84) * mm});
            skLineSegment(sketch, "E430", {"start": v(99.37, 62.51) * mm, "end": v(98.57, 64.75) * mm});
            skLineSegment(sketch, "E431", {"start": v(98.57, 64.75) * mm, "end": v(100.16, 72.48) * mm});
            skLineSegment(sketch, "E432", {"start": v(100.16, 72.48) * mm, "end": v(98.25, 69.37) * mm});
            skLineSegment(sketch, "E433", {"start": v(98.25, 69.37) * mm, "end": v(98, 69.85) * mm});
            skLineSegment(sketch, "E434", {"start": v(98, 69.85) * mm, "end": v(98.27, 70.55) * mm});
            skLineSegment(sketch, "E435", {"start": v(98.27, 70.55) * mm, "end": v(97.13, 73.88) * mm});
            skLineSegment(sketch, "E436", {"start": v(97.13, 73.88) * mm, "end": v(96.1, 73.88) * mm});
            skLineSegment(sketch, "E437", {"start": v(96.1, 73.88) * mm, "end": v(92.1, 74.75) * mm});
            skLineSegment(sketch, "E438", {"start": v(92.1, 74.75) * mm, "end": v(91.96, 75.47) * mm});
            skLineSegment(sketch, "E439", {"start": v(91.96, 75.47) * mm, "end": v(90.31, 75.61) * mm});
            skLineSegment(sketch, "E440", {"start": v(90.31, 75.61) * mm, "end": v(90.13, 76.72) * mm});
            skLineSegment(sketch, "E441", {"start": v(90.13, 76.72) * mm, "end": v(87.02, 75.65) * mm});
            skLineSegment(sketch, "E442", {"start": v(87.02, 75.65) * mm, "end": v(86.98, 73.75) * mm});
            skLineSegment(sketch, "E443", {"start": v(86.98, 73.75) * mm, "end": v(85.66, 71.75) * mm});
            skLineSegment(sketch, "E444", {"start": v(85.66, 71.75) * mm, "end": v(85.98, 68.49) * mm});
            skLineSegment(sketch, "E445", {"start": v(85.98, 68.49) * mm, "end": v(89.74, 65.91) * mm});
            skLineSegment(sketch, "E446", {"start": v(89.74, 65.91) * mm, "end": v(90.78, 62.3) * mm});
            skLineSegment(sketch, "E447", {"start": v(90.78, 62.3) * mm, "end": v(91.7, 61.15) * mm});
            skLineSegment(sketch, "E448", {"start": v(91.7, 61.15) * mm, "end": v(99.37, 62.51) * mm});
            skLineSegment(sketch, "E449", {"start": v(77.09, 63.85) * mm, "end": v(89.6, 65.06) * mm});
            skLineSegment(sketch, "E450", {"start": v(89.6, 65.06) * mm, "end": v(89.4, 65.73) * mm});
            skLineSegment(sketch, "E451", {"start": v(89.4, 65.73) * mm, "end": v(85.54, 68.1) * mm});
            skLineSegment(sketch, "E452", {"start": v(85.54, 68.1) * mm, "end": v(85.17, 71.75) * mm});
            skLineSegment(sketch, "E453", {"start": v(85.17, 71.75) * mm, "end": v(86.62, 73.64) * mm});
            skLineSegment(sketch, "E454", {"start": v(86.62, 73.64) * mm, "end": v(86.42, 75.8) * mm});
            skLineSegment(sketch, "E455", {"start": v(86.42, 75.8) * mm, "end": v(91.68, 80.65) * mm});
            skLineSegment(sketch, "E456", {"start": v(91.68, 80.65) * mm, "end": v(88.64, 81.16) * mm});
            skLineSegment(sketch, "E457", {"start": v(88.64, 81.16) * mm, "end": v(87.48, 80.67) * mm});
            skLineSegment(sketch, "E458", {"start": v(87.48, 80.67) * mm, "end": v(83.62, 82.46) * mm});
            skLineSegment(sketch, "E459", {"start": v(83.62, 82.46) * mm, "end": v(81.89, 81.97) * mm});
            skLineSegment(sketch, "E460", {"start": v(81.89, 81.97) * mm, "end": v(80.25, 82.23) * mm});
            skLineSegment(sketch, "E461", {"start": v(80.25, 82.23) * mm, "end": v(79.44, 83.2) * mm});
            skLineSegment(sketch, "E462", {"start": v(79.44, 83.2) * mm, "end": v(73.59, 82.69) * mm});
            skLineSegment(sketch, "E463", {"start": v(73.59, 82.69) * mm, "end": v(74.08, 78.6) * mm});
            skLineSegment(sketch, "E464", {"start": v(74.08, 78.6) * mm, "end": v(75.06, 77.3) * mm});
            skLineSegment(sketch, "E465", {"start": v(75.06, 77.3) * mm, "end": v(76.24, 72.1) * mm});
            skLineSegment(sketch, "E466", {"start": v(76.24, 72.1) * mm, "end": v(75.46, 70.78) * mm});
            skLineSegment(sketch, "E467", {"start": v(75.46, 70.78) * mm, "end": v(76.53, 69.72) * mm});
            skLineSegment(sketch, "E468", {"start": v(76.53, 69.72) * mm, "end": v(77.09, 63.85) * mm});
            skLineSegment(sketch, "E469", {"start": v(60.82, 54.17) * mm, "end": v(60.82, 41.2) * mm});
            skLineSegment(sketch, "E470", {"start": v(60.82, 41.2) * mm, "end": v(41.34, 41.84) * mm});
            skLineSegment(sketch, "E471", {"start": v(41.34, 41.84) * mm, "end": v(42.4, 54.67) * mm});
            skLineSegment(sketch, "E472", {"start": v(42.4, 54.67) * mm, "end": v(60.82, 54.17) * mm});
            skLineSegment(sketch, "E473", {"start": v(85.17, 14.11) * mm, "end": v(85.08, 16.52) * mm});
            skLineSegment(sketch, "E474", {"start": v(85.08, 16.52) * mm, "end": v(85.62, 17.15) * mm});
            skLineSegment(sketch, "E475", {"start": v(85.62, 17.15) * mm, "end": v(85.5, 20.47) * mm});
            skLineSegment(sketch, "E476", {"start": v(85.5, 20.47) * mm, "end": v(84.58, 21.02) * mm});
            skLineSegment(sketch, "E477", {"start": v(84.58, 21.02) * mm, "end": v(83.67, 26.7) * mm});
            skLineSegment(sketch, "E478", {"start": v(83.67, 26.7) * mm, "end": v(80.33, 27.8) * mm});
            skLineSegment(sketch, "E479", {"start": v(80.33, 27.8) * mm, "end": v(74.74, 27.76) * mm});
            skLineSegment(sketch, "E480", {"start": v(74.74, 27.76) * mm, "end": v(65.4, 30.49) * mm});
            skLineSegment(sketch, "E481", {"start": v(65.4, 30.49) * mm, "end": v(65, 37.79) * mm});
            skLineSegment(sketch, "E482", {"start": v(65, 37.79) * mm, "end": v(57.38, 38.07) * mm});
            skLineSegment(sketch, "E483", {"start": v(57.38, 38.07) * mm, "end": v(56.36, 22.01) * mm});
            skLineSegment(sketch, "E484", {"start": v(56.36, 22.01) * mm, "end": v(46.7, 22.42) * mm});
            skLineSegment(sketch, "E485", {"start": v(46.7, 22.42) * mm, "end": v(46.37, 21.72) * mm});
            skLineSegment(sketch, "E486", {"start": v(46.37, 21.72) * mm, "end": v(45.56, 21.6) * mm});
            skLineSegment(sketch, "E487", {"start": v(45.56, 21.6) * mm, "end": v(50.2, 17.1) * mm});
            skLineSegment(sketch, "E488", {"start": v(50.2, 17.1) * mm, "end": v(51.38, 13.84) * mm});
            skLineSegment(sketch, "E489", {"start": v(51.38, 13.84) * mm, "end": v(56.2, 10.35) * mm});
            skLineSegment(sketch, "E490", {"start": v(56.2, 10.35) * mm, "end": v(57.88, 13.97) * mm});
            skLineSegment(sketch, "E491", {"start": v(57.88, 13.97) * mm, "end": v(60.27, 13.73) * mm});
            skLineSegment(sketch, "E492", {"start": v(60.27, 13.73) * mm, "end": v(62.27, 12.15) * mm});
            skLineSegment(sketch, "E493", {"start": v(62.27, 12.15) * mm, "end": v(63.66, 8.92) * mm});
            skLineSegment(sketch, "E494", {"start": v(63.66, 8.92) * mm, "end": v(65.9, 7.2) * mm});
            skLineSegment(sketch, "E495", {"start": v(65.9, 7.2) * mm, "end": v(67.66, 2.52) * mm});
            skLineSegment(sketch, "E496", {"start": v(67.66, 2.52) * mm, "end": v(74.43, 0.9) * mm});
            skLineSegment(sketch, "E497", {"start": v(74.43, 0.9) * mm, "end": v(75.9, 1.3) * mm});
            skLineSegment(sketch, "E498", {"start": v(75.9, 1.3) * mm, "end": v(74.49, 5.37) * mm});
            skLineSegment(sketch, "E499", {"start": v(74.49, 5.37) * mm, "end": v(77.69, 10.04) * mm});
            skLineSegment(sketch, "E500", {"start": v(77.69, 10.04) * mm, "end": v(78.55, 9.78) * mm});
            skLineSegment(sketch, "E501", {"start": v(78.55, 9.78) * mm, "end": v(84.87, 14.14) * mm});
            skLineSegment(sketch, "E502", {"start": v(84.87, 14.14) * mm, "end": v(85.17, 14.11) * mm});
            skLineSegment(sketch, "E503", {"start": v(82.52, 27.89) * mm, "end": v(82.07, 39.44) * mm});
            skLineSegment(sketch, "E504", {"start": v(82.07, 39.44) * mm, "end": v(57.65, 40.6) * mm});
            skLineSegment(sketch, "E505", {"start": v(57.65, 40.6) * mm, "end": v(57.6, 38.56) * mm});
            skLineSegment(sketch, "E506", {"start": v(57.6, 38.56) * mm, "end": v(65.58, 38.07) * mm});
            skLineSegment(sketch, "E507", {"start": v(65.58, 38.07) * mm, "end": v(65.99, 30.67) * mm});
            skLineSegment(sketch, "E508", {"start": v(65.99, 30.67) * mm, "end": v(74.74, 28.3) * mm});
            skLineSegment(sketch, "E509", {"start": v(74.74, 28.3) * mm, "end": v(80.5, 28.52) * mm});
            skLineSegment(sketch, "E510", {"start": v(80.5, 28.52) * mm, "end": v(82.52, 27.89) * mm});
            skLineSegment(sketch, "E511", {"start": v(83, 38.11) * mm, "end": v(95.44, 39.1) * mm});
            skLineSegment(sketch, "E512", {"start": v(95.44, 39.1) * mm, "end": v(95.32, 36.83) * mm});
            skLineSegment(sketch, "E513", {"start": v(95.32, 36.83) * mm, "end": v(96.67, 36.82) * mm});
            skLineSegment(sketch, "E514", {"start": v(96.67, 36.82) * mm, "end": v(99, 41.84) * mm});
            skLineSegment(sketch, "E515", {"start": v(99, 41.84) * mm, "end": v(97.31, 41.77) * mm});
            skLineSegment(sketch, "E516", {"start": v(97.31, 41.77) * mm, "end": v(97.14, 43.47) * mm});
            skLineSegment(sketch, "E517", {"start": v(97.14, 43.47) * mm, "end": v(94.26, 46.62) * mm});
            skLineSegment(sketch, "E518", {"start": v(94.26, 46.62) * mm, "end": v(94.59, 47.94) * mm});
            skLineSegment(sketch, "E519", {"start": v(94.59, 47.94) * mm, "end": v(94.28, 48.54) * mm});
            skLineSegment(sketch, "E520", {"start": v(94.28, 48.54) * mm, "end": v(93.63, 48.32) * mm});
            skLineSegment(sketch, "E521", {"start": v(93.63, 48.32) * mm, "end": v(91.16, 51.02) * mm});
            skLineSegment(sketch, "E522", {"start": v(91.16, 51.02) * mm, "end": v(89.9, 52.9) * mm});
            skLineSegment(sketch, "E523", {"start": v(89.9, 52.9) * mm, "end": v(90.17, 53.4) * mm});
            skLineSegment(sketch, "E524", {"start": v(90.17, 53.4) * mm, "end": v(89.06, 53.52) * mm});
            skLineSegment(sketch, "E525", {"start": v(89.06, 53.52) * mm, "end": v(79.44, 52.69) * mm});
            skLineSegment(sketch, "E526", {"start": v(79.44, 52.69) * mm, "end": v(80.53, 49.27) * mm});
            skLineSegment(sketch, "E527", {"start": v(80.53, 49.27) * mm, "end": v(82.53, 45.88) * mm});
            skLineSegment(sketch, "E528", {"start": v(82.53, 45.88) * mm, "end": v(83, 38.11) * mm});
            skLineSegment(sketch, "E529", {"start": v(79.64, 52.9) * mm, "end": v(89.9, 54.3) * mm});
            skLineSegment(sketch, "E530", {"start": v(89.9, 54.3) * mm, "end": v(90.44, 53.75) * mm});
            skLineSegment(sketch, "E531", {"start": v(90.44, 53.75) * mm, "end": v(91.43, 55.94) * mm});
            skLineSegment(sketch, "E532", {"start": v(91.43, 55.94) * mm, "end": v(91.02, 57.21) * mm});
            skLineSegment(sketch, "E533", {"start": v(91.02, 57.21) * mm, "end": v(92.77, 58.24) * mm});
            skLineSegment(sketch, "E534", {"start": v(92.77, 58.24) * mm, "end": v(92.77, 59.22) * mm});
            skLineSegment(sketch, "E535", {"start": v(92.77, 59.22) * mm, "end": v(92.3, 59.37) * mm});
            skLineSegment(sketch, "E536", {"start": v(92.3, 59.37) * mm, "end": v(91.58, 60.87) * mm});
            skLineSegment(sketch, "E537", {"start": v(91.58, 60.87) * mm, "end": v(90.25, 61.78) * mm});
            skLineSegment(sketch, "E538", {"start": v(90.25, 61.78) * mm, "end": v(89.76, 64.32) * mm});
            skLineSegment(sketch, "E539", {"start": v(89.76, 64.32) * mm, "end": v(77.6, 63.16) * mm});
            skLineSegment(sketch, "E540", {"start": v(77.6, 63.16) * mm, "end": v(77.07, 63.52) * mm});
            skLineSegment(sketch, "E541", {"start": v(77.07, 63.52) * mm, "end": v(76.5, 62.68) * mm});
            skLineSegment(sketch, "E542", {"start": v(76.5, 62.68) * mm, "end": v(77, 58.97) * mm});
            skLineSegment(sketch, "E543", {"start": v(77, 58.97) * mm, "end": v(79.64, 52.9) * mm});
            skLineSegment(sketch, "E544", {"start": v(41.96, 21.12) * mm, "end": v(42.02, 22.62) * mm});
            skLineSegment(sketch, "E545", {"start": v(42.02, 22.62) * mm, "end": v(45.85, 22.16) * mm});
            skLineSegment(sketch, "E546", {"start": v(45.85, 22.16) * mm, "end": v(46.22, 22.91) * mm});
            skLineSegment(sketch, "E547", {"start": v(46.22, 22.91) * mm, "end": v(56.03, 22.5) * mm});
            skLineSegment(sketch, "E548", {"start": v(56.03, 22.5) * mm, "end": v(56.8, 40.6) * mm});
            skLineSegment(sketch, "E549", {"start": v(56.8, 40.6) * mm, "end": v(41.2, 41.4) * mm});
            skLineSegment(sketch, "E550", {"start": v(41.2, 41.4) * mm, "end": v(39.2, 21.37) * mm});
            skLineSegment(sketch, "E551", {"start": v(39.2, 21.37) * mm, "end": v(41.96, 21.12) * mm});
            skLineSegment(sketch, "E552", {"start": v(61.36, 40.91) * mm, "end": v(81.97, 40.18) * mm});
            skLineSegment(sketch, "E553", {"start": v(81.97, 40.18) * mm, "end": v(81.97, 45.8) * mm});
            skLineSegment(sketch, "E554", {"start": v(81.97, 45.8) * mm, "end": v(80.17, 49.06) * mm});
            skLineSegment(sketch, "E555", {"start": v(80.17, 49.06) * mm, "end": v(79.64, 50.28) * mm});
            skLineSegment(sketch, "E556", {"start": v(79.64, 50.28) * mm, "end": v(61.26, 50.88) * mm});
            skLineSegment(sketch, "E557", {"start": v(61.26, 50.88) * mm, "end": v(61.36, 40.91) * mm});
            skLineSegment(sketch, "E558", {"start": v(79.44, 50.85) * mm, "end": v(78.35, 53.91) * mm});
            skLineSegment(sketch, "E559", {"start": v(78.35, 53.91) * mm, "end": v(76.5, 58.97) * mm});
            skLineSegment(sketch, "E560", {"start": v(76.5, 58.97) * mm, "end": v(76.27, 59.86) * mm});
            skLineSegment(sketch, "E561", {"start": v(76.27, 59.86) * mm, "end": v(74.63, 60.23) * mm});
            skLineSegment(sketch, "E562", {"start": v(74.63, 60.23) * mm, "end": v(73.68, 61.05) * mm});
            skLineSegment(sketch, "E563", {"start": v(73.68, 61.05) * mm, "end": v(72.53, 60.65) * mm});
            skLineSegment(sketch, "E564", {"start": v(72.53, 60.65) * mm, "end": v(70.64, 61.4) * mm});
            skLineSegment(sketch, "E565", {"start": v(70.64, 61.4) * mm, "end": v(56.85, 61.4) * mm});
            skLineSegment(sketch, "E566", {"start": v(56.85, 61.4) * mm, "end": v(56.85, 54.67) * mm});
            skLineSegment(sketch, "E567", {"start": v(56.85, 54.67) * mm, "end": v(61.36, 54.67) * mm});
            skLineSegment(sketch, "E568", {"start": v(61.36, 54.67) * mm, "end": v(61.26, 51.25) * mm});
            skLineSegment(sketch, "E569", {"start": v(61.26, 51.25) * mm, "end": v(79.44, 50.85) * mm});
            skLineSegment(sketch, "E570", {"start": v(56.85, 62.16) * mm, "end": v(70.8, 61.86) * mm});
            skPoint(sketch, "E570.startSnap0", {"position": v(56.85, 58.04) * mm});
            skLineSegment(sketch, "E571", {"start": v(70.8, 61.86) * mm, "end": v(72.49, 61.18) * mm});
            skLineSegment(sketch, "E572", {"start": v(72.49, 61.18) * mm, "end": v(73.68, 61.52) * mm});
            skLineSegment(sketch, "E573", {"start": v(56.85, 62.16) * mm, "end": v(57.12, 71.92) * mm});
            skLineSegment(sketch, "E574", {"start": v(57.12, 71.92) * mm, "end": v(75.25, 71.52) * mm});
            skLineSegment(sketch, "E575", {"start": v(75.25, 71.52) * mm, "end": v(74.82, 70.57) * mm});
            skLineSegment(sketch, "E576", {"start": v(74.82, 70.57) * mm, "end": v(76.01, 69.57) * mm});
            skLineSegment(sketch, "E577", {"start": v(76.01, 69.57) * mm, "end": v(76.36, 63.82) * mm});
            skLineSegment(sketch, "E578", {"start": v(76.36, 63.82) * mm, "end": v(75.9, 62.95) * mm});
            skLineSegment(sketch, "E579", {"start": v(75.9, 62.95) * mm, "end": v(76.15, 60.37) * mm});
            skLineSegment(sketch, "E580", {"start": v(76.15, 60.37) * mm, "end": v(73.68, 61.52) * mm});
            skLineSegment(sketch, "E581", {"start": v(56.47, 54.67) * mm, "end": v(38.06, 55.74) * mm});
            skPoint(sketch, "E581.startSnap0", {"position": v(59.1, 54.67) * mm});
            skLineSegment(sketch, "E582", {"start": v(38.06, 55.74) * mm, "end": v(39.7, 69.13) * mm});
            skLineSegment(sketch, "E583", {"start": v(39.7, 69.13) * mm, "end": v(56.42, 68.06) * mm});
            skLineSegment(sketch, "E584", {"start": v(56.42, 68.06) * mm, "end": v(56.47, 54.67) * mm});
            skLineSegment(sketch, "E585", {"start": v(57.31, 72.33) * mm, "end": v(75.66, 72.1) * mm});
            skLineSegment(sketch, "E586", {"start": v(75.66, 72.1) * mm, "end": v(74.35, 77.62) * mm});
            skLineSegment(sketch, "E587", {"start": v(74.35, 77.62) * mm, "end": v(73.8, 78.34) * mm});
            skLineSegment(sketch, "E588", {"start": v(73.8, 78.34) * mm, "end": v(73.03, 82.61) * mm});
            skLineSegment(sketch, "E589", {"start": v(73.03, 82.61) * mm, "end": v(57.35, 83.12) * mm});
            skLineSegment(sketch, "E590", {"start": v(57.35, 83.12) * mm, "end": v(57.31, 72.33) * mm});
            skLineSegment(sketch, "E591", {"start": v(38.7, 21.37) * mm, "end": v(40.69, 41.4) * mm});
            skLineSegment(sketch, "E592", {"start": v(40.69, 41.4) * mm, "end": v(27.05, 41.84) * mm});
            skLineSegment(sketch, "E593", {"start": v(27.05, 41.84) * mm, "end": v(26.93, 39.85) * mm});
            skLineSegment(sketch, "E594", {"start": v(26.93, 39.85) * mm, "end": v(26.22, 39.42) * mm});
            skLineSegment(sketch, "E595", {"start": v(26.22, 39.42) * mm, "end": v(25.92, 40.06) * mm});
            skLineSegment(sketch, "E596", {"start": v(25.92, 40.06) * mm, "end": v(25.35, 40.27) * mm});
            skLineSegment(sketch, "E597", {"start": v(25.35, 40.27) * mm, "end": v(24.47, 36.19) * mm});
            skLineSegment(sketch, "E598", {"start": v(24.47, 36.19) * mm, "end": v(25.32, 33.12) * mm});
            skLineSegment(sketch, "E599", {"start": v(25.32, 33.12) * mm, "end": v(24.22, 32.16) * mm});
            skLineSegment(sketch, "E600", {"start": v(24.22, 32.16) * mm, "end": v(23.85, 30.36) * mm});
            skLineSegment(sketch, "E601", {"start": v(23.85, 30.36) * mm, "end": v(24.12, 29.37) * mm});
            skLineSegment(sketch, "E602", {"start": v(24.12, 29.37) * mm, "end": v(23.07, 27.58) * mm});
            skLineSegment(sketch, "E603", {"start": v(23.07, 27.58) * mm, "end": v(32.81, 22.49) * mm});
            skLineSegment(sketch, "E604", {"start": v(32.81, 22.49) * mm, "end": v(38.7, 21.37) * mm});
            skLineSegment(sketch, "E605", {"start": v(21.94, 28.9) * mm, "end": v(21.73, 28.42) * mm});
            skLineSegment(sketch, "E606", {"start": v(21.73, 28.42) * mm, "end": v(22.9, 28.02) * mm});
            skLineSegment(sketch, "E607", {"start": v(22.9, 28.02) * mm, "end": v(23.54, 29.6) * mm});
            skLineSegment(sketch, "E608", {"start": v(23.54, 29.6) * mm, "end": v(23.3, 30.2) * mm});
            skLineSegment(sketch, "E609", {"start": v(23.3, 30.2) * mm, "end": v(23.86, 32.5) * mm});
            skLineSegment(sketch, "E610", {"start": v(23.86, 32.5) * mm, "end": v(24.9, 33.25) * mm});
            skLineSegment(sketch, "E611", {"start": v(24.9, 33.25) * mm, "end": v(24.12, 36.08) * mm});
            skLineSegment(sketch, "E612", {"start": v(24.12, 36.08) * mm, "end": v(12.08, 52.54) * mm});
            skLineSegment(sketch, "E613", {"start": v(12.08, 52.54) * mm, "end": v(14.36, 62.59) * mm});
            skLineSegment(sketch, "E614", {"start": v(14.36, 62.59) * mm, "end": v(4.6, 64.8) * mm});
            skLineSegment(sketch, "E615", {"start": v(4.6, 64.8) * mm, "end": v(1.71, 59.55) * mm});
            skLineSegment(sketch, "E616", {"start": v(1.71, 59.55) * mm, "end": v(2.66, 57.66) * mm});
            skLineSegment(sketch, "E617", {"start": v(2.66, 57.66) * mm, "end": v(2.15, 55.43) * mm});
            skLineSegment(sketch, "E618", {"start": v(2.15, 55.43) * mm, "end": v(2.86, 51.24) * mm});
            skLineSegment(sketch, "E619", {"start": v(2.86, 51.24) * mm, "end": v(3.84, 50.03) * mm});
            skLineSegment(sketch, "E620", {"start": v(3.84, 50.03) * mm, "end": v(4.68, 50.63) * mm});
            skLineSegment(sketch, "E621", {"start": v(4.68, 50.63) * mm, "end": v(5.04, 49.35) * mm});
            skLineSegment(sketch, "E622", {"start": v(5.04, 49.35) * mm, "end": v(4.11, 49.69) * mm});
            skLineSegment(sketch, "E623", {"start": v(4.11, 49.69) * mm, "end": v(3.66, 46.98) * mm});
            skLineSegment(sketch, "E624", {"start": v(3.66, 46.98) * mm, "end": v(4.93, 46.67) * mm});
            skLineSegment(sketch, "E625", {"start": v(4.93, 46.67) * mm, "end": v(5.02, 46.3) * mm});
            skLineSegment(sketch, "E626", {"start": v(5.02, 46.3) * mm, "end": v(4.02, 45.54) * mm});
            skLineSegment(sketch, "E627", {"start": v(4.02, 45.54) * mm, "end": v(6.86, 40.22) * mm});
            skLineSegment(sketch, "E628", {"start": v(6.86, 40.22) * mm, "end": v(6.46, 38.6) * mm});
            skLineSegment(sketch, "E629", {"start": v(6.46, 38.6) * mm, "end": v(11.37, 35.58) * mm});
            skLineSegment(sketch, "E630", {"start": v(11.37, 35.58) * mm, "end": v(13.99, 32.42) * mm});
            skLineSegment(sketch, "E631", {"start": v(13.99, 32.42) * mm, "end": v(14.48, 29.94) * mm});
            skLineSegment(sketch, "E632", {"start": v(14.48, 29.94) * mm, "end": v(21.94, 28.9) * mm});
            skLineSegment(sketch, "E633", {"start": v(24.1, 37.04) * mm, "end": v(25.05, 41.43) * mm});
            skLineSegment(sketch, "E634", {"start": v(25.05, 41.43) * mm, "end": v(25.35, 41.36) * mm});
            skLineSegment(sketch, "E635", {"start": v(25.35, 41.36) * mm, "end": v(26.03, 40.27) * mm});
            skLineSegment(sketch, "E636", {"start": v(26.03, 40.27) * mm, "end": v(29.66, 59.89) * mm});
            skLineSegment(sketch, "E637", {"start": v(29.66, 59.89) * mm, "end": v(15.13, 62.64) * mm});
            skLineSegment(sketch, "E638", {"start": v(15.13, 62.64) * mm, "end": v(12.6, 52.45) * mm});
            skLineSegment(sketch, "E639", {"start": v(12.6, 52.45) * mm, "end": v(24.1, 37.04) * mm});
            skLineSegment(sketch, "E640", {"start": v(27.22, 42.62) * mm, "end": v(40.8, 41.65) * mm});
            skLineSegment(sketch, "E641", {"start": v(40.8, 41.65) * mm, "end": v(42, 54.89) * mm});
            skLineSegment(sketch, "E642", {"start": v(42, 54.89) * mm, "end": v(37.64, 55.17) * mm});
            skLineSegment(sketch, "E643", {"start": v(37.64, 55.17) * mm, "end": v(37.75, 58.65) * mm});
            skLineSegment(sketch, "E644", {"start": v(37.75, 58.65) * mm, "end": v(30.24, 59.8) * mm});
            skLineSegment(sketch, "E645", {"start": v(30.24, 59.8) * mm, "end": v(27.22, 42.62) * mm});
            skLineSegment(sketch, "E646", {"start": v(23.25, 61.88) * mm, "end": v(37.7, 59.14) * mm});
            skPoint(sketch, "E646.endSnap0", {"position": v(37.7, 56.9) * mm});
            skLineSegment(sketch, "E647", {"start": v(37.7, 59.14) * mm, "end": v(39.1, 68.36) * mm});
            skLineSegment(sketch, "E648", {"start": v(39.1, 68.36) * mm, "end": v(34.8, 68.56) * mm});
            skLineSegment(sketch, "E649", {"start": v(34.8, 68.56) * mm, "end": v(32.34, 72.36) * mm});
            skLineSegment(sketch, "E650", {"start": v(32.34, 72.36) * mm, "end": v(30.9, 72.4) * mm});
            skLineSegment(sketch, "E651", {"start": v(30.9, 72.4) * mm, "end": v(31.55, 75.61) * mm});
            skLineSegment(sketch, "E652", {"start": v(31.55, 75.61) * mm, "end": v(29.15, 81.47) * mm});
            skLineSegment(sketch, "E653", {"start": v(29.15, 81.47) * mm, "end": v(29.82, 85.81) * mm});
            skLineSegment(sketch, "E654", {"start": v(29.82, 85.81) * mm, "end": v(27.78, 86.23) * mm});
            skLineSegment(sketch, "E655", {"start": v(27.78, 86.23) * mm, "end": v(25.98, 74.48) * mm});
            skLineSegment(sketch, "E656", {"start": v(25.98, 74.48) * mm, "end": v(26.81, 73.4) * mm});
            skLineSegment(sketch, "E657", {"start": v(26.81, 73.4) * mm, "end": v(24.3, 69.72) * mm});
            skLineSegment(sketch, "E658", {"start": v(24.3, 69.72) * mm, "end": v(24.7, 68.26) * mm});
            skLineSegment(sketch, "E659", {"start": v(24.7, 68.26) * mm, "end": v(24.1, 67.28) * mm});
            skLineSegment(sketch, "E660", {"start": v(24.1, 67.28) * mm, "end": v(23.25, 61.88) * mm});
            skLineSegment(sketch, "E661", {"start": v(22.6, 61.88) * mm, "end": v(5, 65.41) * mm});
            skLineSegment(sketch, "E662", {"start": v(5, 65.41) * mm, "end": v(4.2, 67.46) * mm});
            skLineSegment(sketch, "E663", {"start": v(4.2, 67.46) * mm, "end": v(4.82, 68.36) * mm});
            skLineSegment(sketch, "E664", {"start": v(4.82, 68.36) * mm, "end": v(8.68, 77.96) * mm});
            skLineSegment(sketch, "E665", {"start": v(8.68, 77.96) * mm, "end": v(8.97, 78.08) * mm});
            skLineSegment(sketch, "E666", {"start": v(8.97, 78.08) * mm, "end": v(8.9, 79.16) * mm});
            skLineSegment(sketch, "E667", {"start": v(8.9, 79.16) * mm, "end": v(11.18, 78.47) * mm});
            skLineSegment(sketch, "E668", {"start": v(11.18, 78.47) * mm, "end": v(10.95, 77.17) * mm});
            skLineSegment(sketch, "E669", {"start": v(10.95, 77.17) * mm, "end": v(13.17, 76.03) * mm});
            skLineSegment(sketch, "E670", {"start": v(13.17, 76.03) * mm, "end": v(19.25, 76.43) * mm});
            skLineSegment(sketch, "E671", {"start": v(19.25, 76.43) * mm, "end": v(25.04, 74.67) * mm});
            skLineSegment(sketch, "E672", {"start": v(25.04, 74.67) * mm, "end": v(26, 73.3) * mm});
            skLineSegment(sketch, "E673", {"start": v(26, 73.3) * mm, "end": v(23.5, 69.78) * mm});
            skLineSegment(sketch, "E674", {"start": v(23.5, 69.78) * mm, "end": v(23.9, 68.53) * mm});
            skLineSegment(sketch, "E675", {"start": v(23.9, 68.53) * mm, "end": v(23.28, 67) * mm});
            skLineSegment(sketch, "E676", {"start": v(23.28, 67) * mm, "end": v(22.6, 61.88) * mm});
            skLineSegment(sketch, "E677", {"start": v(56.36, 68.56) * mm, "end": v(56.76, 83.12) * mm});
            skLineSegment(sketch, "E678", {"start": v(56.76, 83.12) * mm, "end": v(50.47, 83.12) * mm});
            skLineSegment(sketch, "E679", {"start": v(50.47, 83.12) * mm, "end": v(30.24, 85.81) * mm});
            skLineSegment(sketch, "E680", {"start": v(30.24, 85.81) * mm, "end": v(29.66, 81.51) * mm});
            skLineSegment(sketch, "E681", {"start": v(29.66, 81.51) * mm, "end": v(31.97, 76.3) * mm});
            skLineSegment(sketch, "E682", {"start": v(31.97, 76.3) * mm, "end": v(32.41, 76.34) * mm});
            skLineSegment(sketch, "E683", {"start": v(32.41, 76.34) * mm, "end": v(31.58, 72.86) * mm});
            skLineSegment(sketch, "E684", {"start": v(31.58, 72.86) * mm, "end": v(32.8, 72.93) * mm});
            skLineSegment(sketch, "E685", {"start": v(32.8, 72.93) * mm, "end": v(35.22, 69) * mm});
            skLineSegment(sketch, "E686", {"start": v(35.22, 69) * mm, "end": v(39.1, 68.75) * mm});
            skLineSegment(sketch, "E687", {"start": v(39.1, 68.75) * mm, "end": v(39.17, 69.77) * mm});
            skLineSegment(sketch, "E688", {"start": v(39.17, 69.77) * mm, "end": v(56.36, 68.56) * mm});
            skLineSegment(sketch, "E689", {"start": v(25.04, 75.16) * mm, "end": v(19.27, 76.92) * mm});
            skLineSegment(sketch, "E690", {"start": v(19.27, 76.92) * mm, "end": v(13.6, 76.55) * mm});
            skLineSegment(sketch, "E691", {"start": v(13.6, 76.55) * mm, "end": v(11.81, 77.34) * mm});
            skLineSegment(sketch, "E692", {"start": v(11.81, 77.34) * mm, "end": v(11.97, 78.63) * mm});
            skLineSegment(sketch, "E693", {"start": v(11.97, 78.63) * mm, "end": v(9.02, 79.76) * mm});
            skLineSegment(sketch, "E694", {"start": v(9.02, 79.76) * mm, "end": v(9.39, 84.18) * mm});
            skLineSegment(sketch, "E695", {"start": v(9.39, 84.18) * mm, "end": v(8.92, 86.49) * mm});
            skLineSegment(sketch, "E696", {"start": v(8.92, 86.49) * mm, "end": v(9.9, 88.21) * mm});
            skLineSegment(sketch, "E697", {"start": v(9.9, 88.21) * mm, "end": v(12.37, 86.17) * mm});
            skLineSegment(sketch, "E698", {"start": v(12.37, 86.17) * mm, "end": v(13.15, 87.49) * mm});
            skLineSegment(sketch, "E699", {"start": v(13.15, 87.49) * mm, "end": v(13.21, 89.17) * mm});
            skLineSegment(sketch, "E700", {"start": v(13.21, 89.17) * mm, "end": v(27.12, 86.29) * mm});
            skLineSegment(sketch, "E701", {"start": v(27.12, 86.29) * mm, "end": v(25.04, 75.16) * mm});
            skLineSegment(sketch, "E702", {"start": v(106.87, 18.2) * mm, "end": v(107.82, 18.39) * mm});
            skSolve(sketch);
        }
        {
            var Q0;
            Q0=makeQuery(id+"F0.imprint","IMPRINT",FACE,{"disambiguationData":[TD([[makeQuery(id+"F0.imprint","IMPRINT",EDGE,{"derivedFrom":sQuery(id+"F0.wireOp",EDGE,"E473")}),1.0]])]});
            var Q1;
            Q1=makeQuery(id+"F0.imprint","IMPRINT",FACE,{"disambiguationData":[TD([[makeQuery(id+"F0.imprint","IMPRINT",EDGE,{"derivedFrom":sQuery(id+"F0.wireOp",EDGE,"E544")}),1.0]])]});
            var Q2;
            Q2=makeQuery(id+"F0.imprint","IMPRINT",FACE,{"disambiguationData":[TD([[makeQuery(id+"F0.imprint","IMPRINT",EDGE,{"derivedFrom":sQuery(id+"F0.wireOp",EDGE,"E591")}),1.0]])]});
            var Q3;
            Q3=makeQuery(id+"F0.imprint","IMPRINT",FACE,{"disambiguationData":[TD([[makeQuery(id+"F0.imprint","IMPRINT",EDGE,{"derivedFrom":sQuery(id+"F0.wireOp",EDGE,"E605")}),1.0]])]});
            var Q4;
            Q4=makeQuery(id+"F0.imprint","IMPRINT",FACE,{"disambiguationData":[TD([[makeQuery(id+"F0.imprint","IMPRINT",EDGE,{"derivedFrom":sQuery(id+"F0.wireOp",EDGE,"E633")}),1.0]])]});
            var Q5;
            Q5=makeQuery(id+"F0.imprint","IMPRINT",FACE,{"disambiguationData":[TD([[makeQuery(id+"F0.imprint","IMPRINT",EDGE,{"derivedFrom":sQuery(id+"F0.wireOp",EDGE,"E661")}),-1.0]])]});
            var Q6;
            Q6=makeQuery(id+"F0.imprint","IMPRINT",FACE,{"disambiguationData":[TD([[makeQuery(id+"F0.imprint","IMPRINT",EDGE,{"derivedFrom":sQuery(id+"F0.wireOp",EDGE,"E689")}),-1.0]])]});
            var Q7;
            Q7=makeQuery(id+"F0.imprint","IMPRINT",FACE,{"disambiguationData":[TD([[makeQuery(id+"F0.imprint","IMPRINT",EDGE,{"derivedFrom":sQuery(id+"F0.wireOp",EDGE,"E646")}),1.0]])]});
            var Q8;
            Q8=makeQuery(id+"F0.imprint","IMPRINT",FACE,{"disambiguationData":[TD([[makeQuery(id+"F0.imprint","IMPRINT",EDGE,{"derivedFrom":sQuery(id+"F0.wireOp",EDGE,"E677")}),1.0]])]});
            var Q9;
            Q9=makeQuery(id+"F0.imprint","IMPRINT",FACE,{"disambiguationData":[TD([[makeQuery(id+"F0.imprint","IMPRINT",EDGE,{"derivedFrom":sQuery(id+"F0.wireOp",EDGE,"E640")}),1.0]])]});
            var Q10;
            Q10=makeQuery(id+"F0.imprint","IMPRINT",FACE,{"disambiguationData":[TD([[makeQuery(id+"F0.imprint","IMPRINT",EDGE,{"derivedFrom":sQuery(id+"F0.wireOp",EDGE,"E469")}),-1.0]])]});
            var Q11;
            Q11=makeQuery(id+"F0.imprint","IMPRINT",FACE,{"disambiguationData":[TD([[makeQuery(id+"F0.imprint","IMPRINT",EDGE,{"derivedFrom":sQuery(id+"F0.wireOp",EDGE,"E581")}),-1.0]])]});
            var Q12;
            Q12=makeQuery(id+"F0.imprint","IMPRINT",FACE,{"disambiguationData":[TD([[makeQuery(id+"F0.imprint","IMPRINT",EDGE,{"derivedFrom":sQuery(id+"F0.wireOp",EDGE,"E558")}),1.0]])]});
            var Q13;
            Q13=makeQuery(id+"F0.imprint","IMPRINT",FACE,{"disambiguationData":[TD([[makeQuery(id+"F0.imprint","IMPRINT",EDGE,{"derivedFrom":sQuery(id+"F0.wireOp",EDGE,"E570")}),1.0]])]});
            var Q14;
            Q14=makeQuery(id+"F0.imprint","IMPRINT",FACE,{"disambiguationData":[TD([[makeQuery(id+"F0.imprint","IMPRINT",EDGE,{"derivedFrom":sQuery(id+"F0.wireOp",EDGE,"E585")}),1.0]])]});
            var Q15;
            Q15=makeQuery(id+"F0.imprint","IMPRINT",FACE,{"disambiguationData":[TD([[makeQuery(id+"F0.imprint","IMPRINT",EDGE,{"derivedFrom":sQuery(id+"F0.wireOp",EDGE,"E449")}),1.0]])]});
            var Q16;
            Q16=makeQuery(id+"F0.imprint","IMPRINT",FACE,{"disambiguationData":[TD([[makeQuery(id+"F0.imprint","IMPRINT",EDGE,{"derivedFrom":sQuery(id+"F0.wireOp",EDGE,"E552")}),1.0]])]});
            var Q17;
            Q17=makeQuery(id+"F0.imprint","IMPRINT",FACE,{"disambiguationData":[TD([[makeQuery(id+"F0.imprint","IMPRINT",EDGE,{"derivedFrom":sQuery(id+"F0.wireOp",EDGE,"E503")}),1.0]])]});
            var Q18;
            Q18=makeQuery(id+"F0.imprint","IMPRINT",FACE,{"disambiguationData":[TD([[makeQuery(id+"F0.imprint","IMPRINT",EDGE,{"derivedFrom":sQuery(id+"F0.wireOp",EDGE,"E378")}),-1.0]])]});
            var Q19;
            Q19=makeQuery(id+"F0.imprint","IMPRINT",FACE,{"disambiguationData":[TD([[makeQuery(id+"F0.imprint","IMPRINT",EDGE,{"derivedFrom":sQuery(id+"F0.wireOp",EDGE,"E353")}),1.0]])]});
            var Q20;
            Q20=makeQuery(id+"F0.imprint","IMPRINT",FACE,{"disambiguationData":[TD([[makeQuery(id+"F0.imprint","IMPRINT",EDGE,{"derivedFrom":sQuery(id+"F0.wireOp",EDGE,"E343")}),-1.0]])]});
            var Q21;
            Q21=makeQuery(id+"F0.imprint","IMPRINT",FACE,{"disambiguationData":[TD([[makeQuery(id+"F0.imprint","IMPRINT",EDGE,{"derivedFrom":sQuery(id+"F0.wireOp",EDGE,"E529")}),1.0]])]});
            var Q22;
            Q22=makeQuery(id+"F0.imprint","IMPRINT",FACE,{"disambiguationData":[TD([[makeQuery(id+"F0.imprint","IMPRINT",EDGE,{"derivedFrom":sQuery(id+"F0.wireOp",EDGE,"E430")}),1.0]])]});
            var Q23;
            Q23=makeQuery(id+"F0.imprint","IMPRINT",FACE,{"disambiguationData":[TD([[makeQuery(id+"F0.imprint","IMPRINT",EDGE,{"derivedFrom":sQuery(id+"F0.wireOp",EDGE,"E390")}),1.0]])]});
            var Q24;
            Q24=makeQuery(id+"F0.imprint","IMPRINT",FACE,{"disambiguationData":[TD([[makeQuery(id+"F0.imprint","IMPRINT",EDGE,{"derivedFrom":sQuery(id+"F0.wireOp",EDGE,"E229")}),-1.0]])]});
            var Q25;
            Q25=makeQuery(id+"F0.imprint","IMPRINT",FACE,{"disambiguationData":[TD([[makeQuery(id+"F0.imprint","IMPRINT",EDGE,{"derivedFrom":sQuery(id+"F0.wireOp",EDGE,"E242")}),-1.0]])]});
            var Q26;
            Q26=makeQuery(id+"F0.imprint","IMPRINT",FACE,{"disambiguationData":[TD([[makeQuery(id+"F0.imprint","IMPRINT",EDGE,{"derivedFrom":sQuery(id+"F0.wireOp",EDGE,"E414")}),1.0]])]});
            var Q27;
            Q27=makeQuery(id+"F0.imprint","IMPRINT",FACE,{"disambiguationData":[TD([[makeQuery(id+"F0.imprint","IMPRINT",EDGE,{"derivedFrom":sQuery(id+"F0.wireOp",EDGE,"E511")}),1.0]])]});
            var Q28;
            Q28=makeQuery(id+"F0.imprint","IMPRINT",FACE,{"disambiguationData":[TD([[makeQuery(id+"F0.imprint","IMPRINT",EDGE,{"derivedFrom":sQuery(id+"F0.wireOp",EDGE,"E267")}),1.0]])]});
            var Q29;
            Q29=makeQuery(id+"F0.imprint","IMPRINT",FACE,{"disambiguationData":[TD([[makeQuery(id+"F0.imprint","IMPRINT",EDGE,{"derivedFrom":sQuery(id+"F0.wireOp",EDGE,"E210")}),1.0]])]});
            var Q30;
            Q30=makeQuery(id+"F0.imprint","IMPRINT",FACE,{"disambiguationData":[TD([[makeQuery(id+"F0.imprint","IMPRINT",EDGE,{"derivedFrom":sQuery(id+"F0.wireOp",EDGE,"E139")}),-1.0]])]});
            var Q31;
            Q31=makeQuery(id+"F0.imprint","IMPRINT",FACE,{"disambiguationData":[TD([[makeQuery(id+"F0.imprint","IMPRINT",EDGE,{"derivedFrom":sQuery(id+"F0.wireOp",EDGE,"E189")}),1.0]])]});
            var Q32;
            Q32=makeQuery(id+"F0.imprint","IMPRINT",FACE,{"disambiguationData":[TD([[makeQuery(id+"F0.imprint","IMPRINT",EDGE,{"derivedFrom":sQuery(id+"F0.wireOp",EDGE,"E248")}),-1.0]])]});
            var Q33;
            Q33=makeQuery(id+"F0.imprint","IMPRINT",FACE,{"disambiguationData":[TD([[makeQuery(id+"F0.imprint","IMPRINT",EDGE,{"derivedFrom":sQuery(id+"F0.wireOp",EDGE,"E280")}),1.0]])]});
            var Q34;
            Q34=makeQuery(id+"F0.imprint","IMPRINT",FACE,{"disambiguationData":[TD([[makeQuery(id+"F0.imprint","IMPRINT",EDGE,{"derivedFrom":sQuery(id+"F0.wireOp",EDGE,"E291")}),1.0]])]});
            var Q35;
            Q35=makeQuery(id+"F0.imprint","IMPRINT",FACE,{"disambiguationData":[TD([[makeQuery(id+"F0.imprint","IMPRINT",EDGE,{"derivedFrom":sQuery(id+"F0.wireOp",EDGE,"E305")}),1.0]])]});
            var Q36;
            Q36=makeQuery(id+"F0.imprint","IMPRINT",FACE,{"disambiguationData":[TD([[makeQuery(id+"F0.imprint","IMPRINT",EDGE,{"derivedFrom":sQuery(id+"F0.wireOp",EDGE,"E122")}),-1.0]])]});
            var Q37;
            Q37=makeQuery(id+"F0.imprint","IMPRINT",FACE,{"disambiguationData":[TD([[makeQuery(id+"F0.imprint","IMPRINT",EDGE,{"derivedFrom":sQuery(id+"F0.wireOp",EDGE,"E314")}),-1.0]])]});
            var Q38;
            Q38=makeQuery(id+"F0.imprint","IMPRINT",FACE,{"disambiguationData":[TD([[makeQuery(id+"F0.imprint","IMPRINT",EDGE,{"derivedFrom":sQuery(id+"F0.wireOp",EDGE,"E161")}),-1.0]])]});
            var Q39;
            Q39=makeQuery(id+"F0.imprint","IMPRINT",FACE,{"disambiguationData":[TD([[makeQuery(id+"F0.imprint","IMPRINT",EDGE,{"derivedFrom":sQuery(id+"F0.wireOp",EDGE,"E110")}),1.0]])]});
            var Q40;
            Q40=makeQuery(id+"F0.imprint","IMPRINT",FACE,{"disambiguationData":[TD([[makeQuery(id+"F0.imprint","IMPRINT",EDGE,{"derivedFrom":sQuery(id+"F0.wireOp",EDGE,"E96")}),-1.0]])]});
            var Q41;
            Q41=makeQuery(id+"F0.imprint","IMPRINT",FACE,{"disambiguationData":[TD([[makeQuery(id+"F0.imprint","IMPRINT",EDGE,{"derivedFrom":sQuery(id+"F0.wireOp",EDGE,"E62")}),-1.0]])]});
            var Q42;
            Q42=makeQuery(id+"F0.imprint","IMPRINT",FACE,{"disambiguationData":[TD([[makeQuery(id+"F0.imprint","IMPRINT",EDGE,{"derivedFrom":sQuery(id+"F0.wireOp",EDGE,"E79")}),-1.0]])]});
            var Q43;
            Q43=makeQuery(id+"F0.imprint","IMPRINT",FACE,{"disambiguationData":[TD([[makeQuery(id+"F0.imprint","IMPRINT",EDGE,{"derivedFrom":sQuery(id+"F0.wireOp",EDGE,"E37")}),-1.0]])]});
            var Q44;
            Q44=makeQuery(id+"F0.imprint","IMPRINT",FACE,{"disambiguationData":[TD([[makeQuery(id+"F0.imprint","IMPRINT",EDGE,{"derivedFrom":sQuery(id+"F0.wireOp",EDGE,"E16")}),1.0]])]});
            var Q45;
            Q45=makeQuery(id+"F0.imprint","IMPRINT",FACE,{"disambiguationData":[TD([[makeQuery(id+"F0.imprint","IMPRINT",EDGE,{"derivedFrom":sQuery(id+"F0.wireOp",EDGE,"E30")}),-1.0]])]});
            var Q46;
            Q46=makeQuery(id+"F0.imprint","IMPRINT",FACE,{"disambiguationData":[TD([[makeQuery(id+"F0.imprint","IMPRINT",EDGE,{"derivedFrom":sQuery(id+"F0.wireOp",EDGE,"E0")}),-1.0]])]});
            extrude(context, id + "F1", {"entities" : qUnion([Q0, Q1, Q2, Q3, Q4, Q5, Q6, Q7, Q8, Q9, Q10, Q11, Q12, Q13, Q14, Q15, Q16, Q17, Q18, Q19, Q20, Q21, Q22, Q23, Q24, Q25, Q26, Q27, Q28, Q29, Q30, Q31, Q32, Q33, Q34, Q35, Q36, Q37, Q38, Q39, Q40, Q41, Q42, Q43, Q44, Q45, Q46]), "depth" : 2.54 * mm});
        }
        {
            var Q0;
            Q0=qCreatedBy(makeId("Top.planeOp"),FACE);
            var sketch = newSketch(context, id + "F2", { "sketchPlane" : qUnion([Q0])});
            skLineSegment(sketch, "E703.0", {"start": v(-3.1, 95.28) * mm, "end": v(-3.1, -3.1) * mm});
            skLineSegment(sketch, "E703.1", {"start": v(155.5, 95.28) * mm, "end": v(-3.1, 95.28) * mm});
            skLineSegment(sketch, "E703.2", {"start": v(155.5, 95.28) * mm, "end": v(155.5, -3.1) * mm});
            skLineSegment(sketch, "E703.3", {"start": v(155.5, -3.1) * mm, "end": v(-3.1, -3.1) * mm});
            skLineSegment(sketch, "E704", {"start": v(1.6, 59.59) * mm, "end": v(4.9, 65.43) * mm});
            skLineSegment(sketch, "E705", {"start": v(4.9, 65.43) * mm, "end": v(4.12, 67.46) * mm});
            skLineSegment(sketch, "E706", {"start": v(4.12, 67.46) * mm, "end": v(4.75, 68.35) * mm});
            skLineSegment(sketch, "E707", {"start": v(4.75, 68.35) * mm, "end": v(8.58, 77.98) * mm});
            skLineSegment(sketch, "E708", {"start": v(8.58, 77.98) * mm, "end": v(8.9, 78.15) * mm});
            skLineSegment(sketch, "E709", {"start": v(8.9, 78.15) * mm, "end": v(8.79, 79.55) * mm});
            skLineSegment(sketch, "E710", {"start": v(8.79, 79.55) * mm, "end": v(9.28, 84.1) * mm});
            skLineSegment(sketch, "E711", {"start": v(9.28, 84.1) * mm, "end": v(8.72, 86.5) * mm});
            skLineSegment(sketch, "E712", {"start": v(8.72, 86.5) * mm, "end": v(9.9, 88.34) * mm});
            skLineSegment(sketch, "E713", {"start": v(9.9, 88.34) * mm, "end": v(12.34, 86.32) * mm});
            skLineSegment(sketch, "E714", {"start": v(12.34, 86.32) * mm, "end": v(13.07, 87.5) * mm});
            skLineSegment(sketch, "E715", {"start": v(13.07, 87.5) * mm, "end": v(13.18, 89.2) * mm});
            skLineSegment(sketch, "E716", {"start": v(13.18, 89.2) * mm, "end": v(13.32, 89.2) * mm});
            skLineSegment(sketch, "E717", {"start": v(13.32, 89.2) * mm, "end": v(33.03, 85.55) * mm});
            skLineSegment(sketch, "E718", {"start": v(33.03, 85.55) * mm, "end": v(50.56, 83.52) * mm});
            skLineSegment(sketch, "E719", {"start": v(50.56, 83.52) * mm, "end": v(73.64, 83.08) * mm});
            skLineSegment(sketch, "E720", {"start": v(73.64, 83.08) * mm, "end": v(79.32, 83.58) * mm});
            skLineSegment(sketch, "E721", {"start": v(79.32, 83.58) * mm, "end": v(80.36, 82.32) * mm});
            skLineSegment(sketch, "E722", {"start": v(80.36, 82.32) * mm, "end": v(81.87, 82.1) * mm});
            skLineSegment(sketch, "E723", {"start": v(81.87, 82.1) * mm, "end": v(83.55, 82.62) * mm});
            skLineSegment(sketch, "E724", {"start": v(83.55, 82.62) * mm, "end": v(87.53, 80.81) * mm});
            skLineSegment(sketch, "E725", {"start": v(87.53, 80.81) * mm, "end": v(88.61, 81.31) * mm});
            skLineSegment(sketch, "E726", {"start": v(88.61, 81.31) * mm, "end": v(91.86, 80.7) * mm});
            skLineSegment(sketch, "E727", {"start": v(91.86, 80.7) * mm, "end": v(86.95, 76.06) * mm});
            skLineSegment(sketch, "E728", {"start": v(86.95, 76.06) * mm, "end": v(87.18, 75.81) * mm});
            skLineSegment(sketch, "E729", {"start": v(87.18, 75.81) * mm, "end": v(90.22, 76.86) * mm});
            skLineSegment(sketch, "E730", {"start": v(90.22, 76.86) * mm, "end": v(90.4, 75.68) * mm});
            skLineSegment(sketch, "E731", {"start": v(90.4, 75.68) * mm, "end": v(92, 75.68) * mm});
            skLineSegment(sketch, "E732", {"start": v(92, 75.68) * mm, "end": v(92.18, 74.9) * mm});
            skLineSegment(sketch, "E733", {"start": v(92.18, 74.9) * mm, "end": v(96.1, 73.98) * mm});
            skLineSegment(sketch, "E734", {"start": v(96.1, 73.98) * mm, "end": v(97.18, 73.98) * mm});
            skLineSegment(sketch, "E735", {"start": v(97.18, 73.98) * mm, "end": v(98.43, 70.6) * mm});
            skLineSegment(sketch, "E736", {"start": v(98.43, 70.6) * mm, "end": v(98.27, 69.76) * mm});
            skLineSegment(sketch, "E737", {"start": v(98.27, 69.76) * mm, "end": v(100.26, 72.79) * mm});
            skLineSegment(sketch, "E738", {"start": v(100.26, 72.79) * mm, "end": v(99, 64.73) * mm});
            skLineSegment(sketch, "E739", {"start": v(99, 64.73) * mm, "end": v(100.12, 59.88) * mm});
            skLineSegment(sketch, "E740", {"start": v(100.12, 59.88) * mm, "end": v(102.22, 59.64) * mm});
            skLineSegment(sketch, "E741", {"start": v(102.22, 59.64) * mm, "end": v(102.5, 61.16) * mm});
            skLineSegment(sketch, "E742", {"start": v(102.5, 61.16) * mm, "end": v(103.82, 63.65) * mm});
            skLineSegment(sketch, "E743", {"start": v(103.82, 63.65) * mm, "end": v(102.15, 69.31) * mm});
            skLineSegment(sketch, "E744", {"start": v(102.15, 69.31) * mm, "end": v(104.53, 74.25) * mm});
            skLineSegment(sketch, "E745", {"start": v(104.53, 74.25) * mm, "end": v(104.53, 72.9) * mm});
            skLineSegment(sketch, "E746", {"start": v(104.53, 72.9) * mm, "end": v(104.75, 72.86) * mm});
            skLineSegment(sketch, "E747", {"start": v(104.75, 72.86) * mm, "end": v(105.64, 75.54) * mm});
            skLineSegment(sketch, "E748", {"start": v(105.64, 75.54) * mm, "end": v(109.8, 74.36) * mm});
            skLineSegment(sketch, "E749", {"start": v(109.8, 74.36) * mm, "end": v(110.77, 71.66) * mm});
            skLineSegment(sketch, "E750", {"start": v(110.77, 71.66) * mm, "end": v(109.55, 68.63) * mm});
            skLineSegment(sketch, "E751", {"start": v(109.55, 68.63) * mm, "end": v(110.33, 68.31) * mm});
            skLineSegment(sketch, "E752", {"start": v(110.33, 68.31) * mm, "end": v(111.76, 70.77) * mm});
            skLineSegment(sketch, "E753", {"start": v(111.76, 70.77) * mm, "end": v(113.61, 67.7) * mm});
            skLineSegment(sketch, "E754", {"start": v(113.61, 67.7) * mm, "end": v(113.96, 66) * mm});
            skLineSegment(sketch, "E755", {"start": v(113.96, 66) * mm, "end": v(112.24, 61.27) * mm});
            skLineSegment(sketch, "E756", {"start": v(112.24, 61.27) * mm, "end": v(113.7, 60.26) * mm});
            skLineSegment(sketch, "E757", {"start": v(113.7, 60.26) * mm, "end": v(116.81, 61.05) * mm});
            skLineSegment(sketch, "E758", {"start": v(116.81, 61.05) * mm, "end": v(117.35, 62.54) * mm});
            skLineSegment(sketch, "E759", {"start": v(117.35, 62.54) * mm, "end": v(118.23, 62.84) * mm});
            skLineSegment(sketch, "E760", {"start": v(118.23, 62.84) * mm, "end": v(119.56, 63.86) * mm});
            skLineSegment(sketch, "E761", {"start": v(119.56, 63.86) * mm, "end": v(120.07, 63.86) * mm});
            skLineSegment(sketch, "E762", {"start": v(120.07, 63.86) * mm, "end": v(122.6, 66.92) * mm});
            skLineSegment(sketch, "E763", {"start": v(122.6, 66.92) * mm, "end": v(124.29, 68.76) * mm});
            skLineSegment(sketch, "E764", {"start": v(124.29, 68.76) * mm, "end": v(123.03, 69.87) * mm});
            skLineSegment(sketch, "E765", {"start": v(123.03, 69.87) * mm, "end": v(124.89, 71.35) * mm});
            skLineSegment(sketch, "E766", {"start": v(124.89, 71.35) * mm, "end": v(126.64, 71.4) * mm});
            skLineSegment(sketch, "E767", {"start": v(126.64, 71.4) * mm, "end": v(128.91, 72.62) * mm});
            skLineSegment(sketch, "E768", {"start": v(128.91, 72.62) * mm, "end": v(128.91, 75.67) * mm});
            skLineSegment(sketch, "E769", {"start": v(128.91, 75.67) * mm, "end": v(129.82, 75.67) * mm});
            skLineSegment(sketch, "E770", {"start": v(129.82, 75.67) * mm, "end": v(130.56, 78.26) * mm});
            skLineSegment(sketch, "E771", {"start": v(130.56, 78.26) * mm, "end": v(136.24, 80.19) * mm});
            skLineSegment(sketch, "E772", {"start": v(136.24, 80.19) * mm, "end": v(139.54, 81.31) * mm});
            skLineSegment(sketch, "E773", {"start": v(139.54, 81.31) * mm, "end": v(140.63, 82.5) * mm});
            skLineSegment(sketch, "E774", {"start": v(140.63, 82.5) * mm, "end": v(140.84, 82.1) * mm});
            skLineSegment(sketch, "E775", {"start": v(140.84, 82.1) * mm, "end": v(142.04, 83.17) * mm});
            skLineSegment(sketch, "E776", {"start": v(142.04, 83.17) * mm, "end": v(143.28, 85.9) * mm});
            skLineSegment(sketch, "E777", {"start": v(143.28, 85.9) * mm, "end": v(142.73, 86.52) * mm});
            skLineSegment(sketch, "E778", {"start": v(142.73, 86.52) * mm, "end": v(143.26, 87.93) * mm});
            skLineSegment(sketch, "E779", {"start": v(143.26, 87.93) * mm, "end": v(142.64, 88.7) * mm});
            skLineSegment(sketch, "E780", {"start": v(142.64, 88.7) * mm, "end": v(143.89, 91.66) * mm});
            skLineSegment(sketch, "E781", {"start": v(143.89, 91.66) * mm, "end": v(144.88, 91.66) * mm});
            skLineSegment(sketch, "E782", {"start": v(144.88, 91.66) * mm, "end": v(145.97, 92.1) * mm});
            skLineSegment(sketch, "E783", {"start": v(145.97, 92.1) * mm, "end": v(148.48, 91.53) * mm});
            skLineSegment(sketch, "E784", {"start": v(148.48, 91.53) * mm, "end": v(150.14, 87.5) * mm});
            skLineSegment(sketch, "E785", {"start": v(150.14, 87.5) * mm, "end": v(150.97, 86.4) * mm});
            skLineSegment(sketch, "E786", {"start": v(150.97, 86.4) * mm, "end": v(151.7, 86.65) * mm});
            skLineSegment(sketch, "E787", {"start": v(151.7, 86.65) * mm, "end": v(152.35, 84.87) * mm});
            skLineSegment(sketch, "E788", {"start": v(152.35, 84.87) * mm, "end": v(147.09, 78.5) * mm});
            skLineSegment(sketch, "E789", {"start": v(147.09, 78.5) * mm, "end": v(145.68, 75.87) * mm});
            skLineSegment(sketch, "E790", {"start": v(145.68, 75.87) * mm, "end": v(145.38, 75.81) * mm});
            skLineSegment(sketch, "E791", {"start": v(145.38, 75.81) * mm, "end": v(145.14, 74.5) * mm});
            skLineSegment(sketch, "E792", {"start": v(145.14, 74.5) * mm, "end": v(145.84, 73.86) * mm});
            skLineSegment(sketch, "E793", {"start": v(145.84, 73.86) * mm, "end": v(145.84, 73.17) * mm});
            skLineSegment(sketch, "E794", {"start": v(145.84, 73.17) * mm, "end": v(145.68, 72.99) * mm});
            skLineSegment(sketch, "E795", {"start": v(145.68, 72.99) * mm, "end": v(145.58, 72.5) * mm});
            skLineSegment(sketch, "E796", {"start": v(145.58, 72.5) * mm, "end": v(146.02, 72.5) * mm});
            skLineSegment(sketch, "E797", {"start": v(146.02, 72.5) * mm, "end": v(146.72, 71.7) * mm});
            skLineSegment(sketch, "E798", {"start": v(146.72, 71.7) * mm, "end": v(147.35, 71.32) * mm});
            skLineSegment(sketch, "E799", {"start": v(147.35, 71.32) * mm, "end": v(147.8, 71.28) * mm});
            skLineSegment(sketch, "E800", {"start": v(147.8, 71.28) * mm, "end": v(147.38, 72.31) * mm});
            skLineSegment(sketch, "E801", {"start": v(147.38, 72.31) * mm, "end": v(148.15, 72.31) * mm});
            skLineSegment(sketch, "E802", {"start": v(148.15, 72.31) * mm, "end": v(148.8, 71.51) * mm});
            skLineSegment(sketch, "E803", {"start": v(148.8, 71.51) * mm, "end": v(148.12, 69.78) * mm});
            skLineSegment(sketch, "E804", {"start": v(148.12, 69.78) * mm, "end": v(147.05, 69.78) * mm});
            skLineSegment(sketch, "E805", {"start": v(147.05, 69.78) * mm, "end": v(146.8, 70.2) * mm});
            skLineSegment(sketch, "E806", {"start": v(146.8, 70.2) * mm, "end": v(146.64, 70.2) * mm});
            skLineSegment(sketch, "E807", {"start": v(146.64, 70.2) * mm, "end": v(145.9, 69.31) * mm});
            skLineSegment(sketch, "E808", {"start": v(145.9, 69.31) * mm, "end": v(145.76, 68.58) * mm});
            skLineSegment(sketch, "E809", {"start": v(145.76, 68.58) * mm, "end": v(144.46, 67.28) * mm});
            skLineSegment(sketch, "E810", {"start": v(144.46, 67.28) * mm, "end": v(144.6, 66.82) * mm});
            skLineSegment(sketch, "E811", {"start": v(144.6, 66.82) * mm, "end": v(143.63, 67.64) * mm});
            skLineSegment(sketch, "E812", {"start": v(143.63, 67.64) * mm, "end": v(143.7, 66.92) * mm});
            skLineSegment(sketch, "E813", {"start": v(143.7, 66.92) * mm, "end": v(139.68, 65.25) * mm});
            skLineSegment(sketch, "E814", {"start": v(139.68, 65.25) * mm, "end": v(138.4, 63.4) * mm});
            skLineSegment(sketch, "E815", {"start": v(138.4, 63.4) * mm, "end": v(138.9, 62.73) * mm});
            skLineSegment(sketch, "E816", {"start": v(138.9, 62.73) * mm, "end": v(138.4, 57.37) * mm});
            skLineSegment(sketch, "E817", {"start": v(138.4, 57.37) * mm, "end": v(136.03, 58.62) * mm});
            skLineSegment(sketch, "E818", {"start": v(136.03, 58.62) * mm, "end": v(135.87, 58.32) * mm});
            skLineSegment(sketch, "E819", {"start": v(135.87, 58.32) * mm, "end": v(136.42, 57.61) * mm});
            skLineSegment(sketch, "E820", {"start": v(136.42, 57.61) * mm, "end": v(137.03, 56.65) * mm});
            skLineSegment(sketch, "E821", {"start": v(137.03, 56.65) * mm, "end": v(137.98, 55.9) * mm});
            skLineSegment(sketch, "E822", {"start": v(137.98, 55.9) * mm, "end": v(137.58, 54.78) * mm});
            skLineSegment(sketch, "E823", {"start": v(137.58, 54.78) * mm, "end": v(137.8, 54.09) * mm});
            skLineSegment(sketch, "E824", {"start": v(137.8, 54.09) * mm, "end": v(137.31, 53.2) * mm});
            skLineSegment(sketch, "E825", {"start": v(137.31, 53.2) * mm, "end": v(137, 52.6) * mm});
            skLineSegment(sketch, "E826", {"start": v(137, 52.6) * mm, "end": v(135.56, 52.2) * mm});
            skLineSegment(sketch, "E827", {"start": v(135.56, 52.2) * mm, "end": v(134.36, 51.27) * mm});
            skLineSegment(sketch, "E828", {"start": v(134.36, 51.27) * mm, "end": v(134.55, 48.77) * mm});
            skLineSegment(sketch, "E829", {"start": v(134.55, 48.77) * mm, "end": v(135.7, 48.6) * mm});
            skLineSegment(sketch, "E830", {"start": v(135.7, 48.6) * mm, "end": v(136.03, 47.47) * mm});
            skLineSegment(sketch, "E831", {"start": v(136.03, 47.47) * mm, "end": v(135.7, 44.75) * mm});
            skLineSegment(sketch, "E832", {"start": v(135.7, 44.75) * mm, "end": v(137.2, 43.94) * mm});
            skLineSegment(sketch, "E833", {"start": v(137.2, 43.94) * mm, "end": v(135.83, 42) * mm});
            skLineSegment(sketch, "E834", {"start": v(135.83, 42) * mm, "end": v(135.83, 41.39) * mm});
            skLineSegment(sketch, "E835", {"start": v(135.83, 41.39) * mm, "end": v(132.35, 37.94) * mm});
            skLineSegment(sketch, "E836", {"start": v(132.35, 37.94) * mm, "end": v(131.96, 36.14) * mm});
            skLineSegment(sketch, "E837", {"start": v(131.96, 36.14) * mm, "end": v(130.02, 35.34) * mm});
            skLineSegment(sketch, "E838", {"start": v(130.02, 35.34) * mm, "end": v(130.33, 34.27) * mm});
            skLineSegment(sketch, "E839", {"start": v(130.33, 34.27) * mm, "end": v(129.33, 33.98) * mm});
            skLineSegment(sketch, "E840", {"start": v(129.33, 33.98) * mm, "end": v(128.09, 31.14) * mm});
            skLineSegment(sketch, "E841", {"start": v(128.09, 31.14) * mm, "end": v(124.36, 25.98) * mm});
            skLineSegment(sketch, "E842", {"start": v(124.36, 25.98) * mm, "end": v(123.72, 23.88) * mm});
            skLineSegment(sketch, "E843", {"start": v(123.72, 23.88) * mm, "end": v(124.45, 22.43) * mm});
            skLineSegment(sketch, "E844", {"start": v(124.45, 22.43) * mm, "end": v(125.08, 19.21) * mm});
            skLineSegment(sketch, "E845", {"start": v(125.08, 19.21) * mm, "end": v(128.08, 15.3) * mm});
            skLineSegment(sketch, "E846", {"start": v(128.08, 15.3) * mm, "end": v(127.88, 14.48) * mm});
            skLineSegment(sketch, "E847", {"start": v(127.88, 14.48) * mm, "end": v(130.5, 10.43) * mm});
            skLineSegment(sketch, "E848", {"start": v(130.5, 10.43) * mm, "end": v(130.76, 4.78) * mm});
            skLineSegment(sketch, "E849", {"start": v(130.76, 4.78) * mm, "end": v(130.37, 3) * mm});
            skLineSegment(sketch, "E850", {"start": v(130.37, 3) * mm, "end": v(126.87, 0.86) * mm});
            skLineSegment(sketch, "E851", {"start": v(126.87, 0.86) * mm, "end": v(126.54, 0.86) * mm});
            skLineSegment(sketch, "E852", {"start": v(126.54, 0.86) * mm, "end": v(129.41, 3.68) * mm});
            skLineSegment(sketch, "E853", {"start": v(129.41, 3.68) * mm, "end": v(129.41, 4.27) * mm});
            skLineSegment(sketch, "E854", {"start": v(129.41, 4.27) * mm, "end": v(128.67, 3.7) * mm});
            skLineSegment(sketch, "E855", {"start": v(128.67, 3.7) * mm, "end": v(123.92, 8.05) * mm});
            skLineSegment(sketch, "E856", {"start": v(123.92, 8.05) * mm, "end": v(121.54, 10.8) * mm});
            skLineSegment(sketch, "E857", {"start": v(121.54, 10.8) * mm, "end": v(120.46, 15.37) * mm});
            skLineSegment(sketch, "E858", {"start": v(120.46, 15.37) * mm, "end": v(117.1, 18) * mm});
            skLineSegment(sketch, "E859", {"start": v(117.1, 18) * mm, "end": v(116.58, 17.92) * mm});
            skLineSegment(sketch, "E860", {"start": v(116.58, 17.92) * mm, "end": v(116.58, 17.23) * mm});
            skLineSegment(sketch, "E861", {"start": v(116.58, 17.23) * mm, "end": v(113.3, 16.48) * mm});
            skLineSegment(sketch, "E862", {"start": v(113.3, 16.48) * mm, "end": v(111.82, 17.85) * mm});
            skLineSegment(sketch, "E863", {"start": v(111.82, 17.85) * mm, "end": v(109.7, 18.64) * mm});
            skLineSegment(sketch, "E864", {"start": v(109.7, 18.64) * mm, "end": v(108.18, 17.9) * mm});
            skLineSegment(sketch, "E865", {"start": v(108.18, 17.9) * mm, "end": v(107.86, 18.32) * mm});
            skLineSegment(sketch, "E866", {"start": v(107.86, 18.32) * mm, "end": v(106.82, 18.13) * mm});
            skLineSegment(sketch, "E867", {"start": v(106.82, 18.13) * mm, "end": v(106.33, 18.13) * mm});
            skLineSegment(sketch, "E868", {"start": v(106.33, 18.13) * mm, "end": v(104.64, 17.64) * mm});
            skLineSegment(sketch, "E869", {"start": v(104.64, 17.64) * mm, "end": v(103.39, 17.97) * mm});
            skLineSegment(sketch, "E870", {"start": v(103.39, 17.97) * mm, "end": v(99.68, 17.97) * mm});
            skLineSegment(sketch, "E871", {"start": v(99.68, 17.97) * mm, "end": v(99.43, 16.72) * mm});
            skLineSegment(sketch, "E872", {"start": v(99.43, 16.72) * mm, "end": v(100.16, 16.48) * mm});
            skLineSegment(sketch, "E873", {"start": v(100.16, 16.48) * mm, "end": v(98.83, 14.72) * mm});
            skLineSegment(sketch, "E874", {"start": v(98.83, 14.72) * mm, "end": v(100.5, 13.05) * mm});
            skLineSegment(sketch, "E875", {"start": v(100.5, 13.05) * mm, "end": v(99.43, 11.96) * mm});
            skLineSegment(sketch, "E876", {"start": v(99.43, 11.96) * mm, "end": v(97.48, 13.64) * mm});
            skLineSegment(sketch, "E877", {"start": v(97.48, 13.64) * mm, "end": v(97.27, 12.6) * mm});
            skLineSegment(sketch, "E878", {"start": v(97.27, 12.6) * mm, "end": v(96.02, 12.9) * mm});
            skLineSegment(sketch, "E879", {"start": v(96.02, 12.9) * mm, "end": v(95.8, 12) * mm});
            skLineSegment(sketch, "E880", {"start": v(95.8, 12) * mm, "end": v(91.97, 13.8) * mm});
            skLineSegment(sketch, "E881", {"start": v(91.97, 13.8) * mm, "end": v(89.34, 12.77) * mm});
            skLineSegment(sketch, "E882", {"start": v(89.34, 12.77) * mm, "end": v(89.22, 13.62) * mm});
            skLineSegment(sketch, "E883", {"start": v(89.22, 13.62) * mm, "end": v(84.96, 13.8) * mm});
            skLineSegment(sketch, "E884", {"start": v(84.96, 13.8) * mm, "end": v(78.77, 9.55) * mm});
            skLineSegment(sketch, "E885", {"start": v(78.77, 9.55) * mm, "end": v(75.06, 5.37) * mm});
            skLineSegment(sketch, "E886", {"start": v(75.06, 5.37) * mm, "end": v(76.63, 1.1) * mm});
            skLineSegment(sketch, "E887", {"start": v(76.63, 1.1) * mm, "end": v(74.42, 0.28) * mm});
            skLineSegment(sketch, "E888", {"start": v(74.42, 0.28) * mm, "end": v(66.8, 2.01) * mm});
            skLineSegment(sketch, "E889", {"start": v(66.8, 2.01) * mm, "end": v(65.63, 6.73) * mm});
            skLineSegment(sketch, "E890", {"start": v(65.63, 6.73) * mm, "end": v(63.18, 8.17) * mm});
            skLineSegment(sketch, "E891", {"start": v(63.18, 8.17) * mm, "end": v(61.74, 11.61) * mm});
            skLineSegment(sketch, "E892", {"start": v(61.74, 11.61) * mm, "end": v(60.08, 12.88) * mm});
            skLineSegment(sketch, "E893", {"start": v(60.08, 12.88) * mm, "end": v(58.33, 12.88) * mm});
            skLineSegment(sketch, "E894", {"start": v(58.33, 12.88) * mm, "end": v(56.44, 9.35) * mm});
            skLineSegment(sketch, "E895", {"start": v(56.44, 9.35) * mm, "end": v(50.95, 13.5) * mm});
            skLineSegment(sketch, "E896", {"start": v(50.95, 13.5) * mm, "end": v(49.97, 16.85) * mm});
            skLineSegment(sketch, "E897", {"start": v(49.97, 16.85) * mm, "end": v(45.07, 21.9) * mm});
            skLineSegment(sketch, "E898", {"start": v(45.07, 21.9) * mm, "end": v(43.31, 21.9) * mm});
            skLineSegment(sketch, "E899", {"start": v(43.31, 21.9) * mm, "end": v(42.67, 19.97) * mm});
            skLineSegment(sketch, "E900", {"start": v(42.67, 19.97) * mm, "end": v(32.54, 22) * mm});
            skLineSegment(sketch, "E901", {"start": v(32.54, 22) * mm, "end": v(20.63, 28.76) * mm});
            skLineSegment(sketch, "E902", {"start": v(20.63, 28.76) * mm, "end": v(14.39, 29.53) * mm});
            skLineSegment(sketch, "E903", {"start": v(14.39, 29.53) * mm, "end": v(13.57, 32.36) * mm});
            skLineSegment(sketch, "E904", {"start": v(13.57, 32.36) * mm, "end": v(11.14, 35.24) * mm});
            skLineSegment(sketch, "E905", {"start": v(11.14, 35.24) * mm, "end": v(6.16, 38.5) * mm});
            skLineSegment(sketch, "E906", {"start": v(6.16, 38.5) * mm, "end": v(6.47, 40.09) * mm});
            skLineSegment(sketch, "E907", {"start": v(6.47, 40.09) * mm, "end": v(3.71, 45.49) * mm});
            skLineSegment(sketch, "E908", {"start": v(3.71, 45.49) * mm, "end": v(4.67, 46.34) * mm});
            skLineSegment(sketch, "E909", {"start": v(4.67, 46.34) * mm, "end": v(3.4, 46.68) * mm});
            skLineSegment(sketch, "E910", {"start": v(3.4, 46.68) * mm, "end": v(3.94, 49.61) * mm});
            skLineSegment(sketch, "E911", {"start": v(3.94, 49.61) * mm, "end": v(4.2, 49.94) * mm});
            skLineSegment(sketch, "E912", {"start": v(4.2, 49.94) * mm, "end": v(4.64, 49.7) * mm});
            skLineSegment(sketch, "E913", {"start": v(4.64, 49.7) * mm, "end": v(4.57, 50.3) * mm});
            skLineSegment(sketch, "E914", {"start": v(4.57, 50.3) * mm, "end": v(3.76, 49.88) * mm});
            skLineSegment(sketch, "E915", {"start": v(3.76, 49.88) * mm, "end": v(2.77, 51.18) * mm});
            skLineSegment(sketch, "E916", {"start": v(2.77, 51.18) * mm, "end": v(1.92, 55.4) * mm});
            skLineSegment(sketch, "E917", {"start": v(1.92, 55.4) * mm, "end": v(2.52, 57.62) * mm});
            skLineSegment(sketch, "E918", {"start": v(2.52, 57.62) * mm, "end": v(1.6, 59.59) * mm});
            skSolve(sketch);
        }
        {
            var Q0;
            Q0=qCreatedBy(makeId("Top.planeOp"),FACE);
            var sketch = newSketch(context, id + "F3", { "sketchPlane" : qUnion([Q0])});
            skLineSegment(sketch, "E919", {"start": v(0, 0) * mm, "end": v(0, 92.19) * mm});
            skLineSegment(sketch, "E920", {"start": v(0, 92.19) * mm, "end": v(152.42, 92.19) * mm});
            skLineSegment(sketch, "E921", {"start": v(152.42, 92.19) * mm, "end": v(152.42, 0) * mm});
            skLineSegment(sketch, "E922", {"start": v(152.42, 0) * mm, "end": v(0, 0) * mm});
            skSolve(sketch);
        }
        {
            var Q0;
            Q0 = qSketchRegion(id + "F3", true);
            extrude(context, id + "F4", {"entities" : qUnion([Q0]), "oppositeDirection" : true, "depth" : 2.54 * mm});
        }
        {
            var Q0;
            Q0=makeQuery(id+"F2.imprint","IMPRINT",FACE,{"disambiguationData":[TD([[makeQuery(id+"F2.imprint","IMPRINT",EDGE,{"derivedFrom":sQuery(id+"F2.wireOp",EDGE,"E703.0")}),1.0]])]});
            extrude(context, id + "F5", {"entities" : qUnion([Q0]), "operationType" : NewBodyOperationType.ADD, "depth" : 2.54 * mm});
        }
        {
            var Q0;
            Q0=makeQuery(id+"F5.opExtrude","CAP_FACE",FACE,{"disambiguationData":[OSD([sQuery(id+"F2.wireOp",EDGE,"E703.0"),sQuery(id+"F2.wireOp",EDGE,"E703.1"),sQuery(id+"F2.wireOp",EDGE,"E703.2"),sQuery(id+"F2.wireOp",EDGE,"E703.3"),sQuery(id+"F2.wireOp",EDGE,"E704"),sQuery(id+"F2.wireOp",EDGE,"E705"),sQuery(id+"F2.wireOp",EDGE,"E706"),sQuery(id+"F2.wireOp",EDGE,"E707"),sQuery(id+"F2.wireOp",EDGE,"E708"),sQuery(id+"F2.wireOp",EDGE,"E709"),sQuery(id+"F2.wireOp",EDGE,"E710"),sQuery(id+"F2.wireOp",EDGE,"E711"),sQuery(id+"F2.wireOp",EDGE,"E712"),sQuery(id+"F2.wireOp",EDGE,"E713"),sQuery(id+"F2.wireOp",EDGE,"E714"),sQuery(id+"F2.wireOp",EDGE,"E715"),sQuery(id+"F2.wireOp",EDGE,"E716"),sQuery(id+"F2.wireOp",EDGE,"E717"),sQuery(id+"F2.wireOp",EDGE,"E718"),sQuery(id+"F2.wireOp",EDGE,"E719"),sQuery(id+"F2.wireOp",EDGE,"E720"),sQuery(id+"F2.wireOp",EDGE,"E721"),sQuery(id+"F2.wireOp",EDGE,"E722"),sQuery(id+"F2.wireOp",EDGE,"E723"),sQuery(id+"F2.wireOp",EDGE,"E724"),sQuery(id+"F2.wireOp",EDGE,"E725"),sQuery(id+"F2.wireOp",EDGE,"E726"),sQuery(id+"F2.wireOp",EDGE,"E727"),sQuery(id+"F2.wireOp",EDGE,"E728"),sQuery(id+"F2.wireOp",EDGE,"E729"),sQuery(id+"F2.wireOp",EDGE,"E730"),sQuery(id+"F2.wireOp",EDGE,"E731"),sQuery(id+"F2.wireOp",EDGE,"E732"),sQuery(id+"F2.wireOp",EDGE,"E733"),sQuery(id+"F2.wireOp",EDGE,"E734"),sQuery(id+"F2.wireOp",EDGE,"E735"),sQuery(id+"F2.wireOp",EDGE,"E736"),sQuery(id+"F2.wireOp",EDGE,"E737"),sQuery(id+"F2.wireOp",EDGE,"E738"),sQuery(id+"F2.wireOp",EDGE,"E739"),sQuery(id+"F2.wireOp",EDGE,"E740"),sQuery(id+"F2.wireOp",EDGE,"E741"),sQuery(id+"F2.wireOp",EDGE,"E742"),sQuery(id+"F2.wireOp",EDGE,"E743"),sQuery(id+"F2.wireOp",EDGE,"E744"),sQuery(id+"F2.wireOp",EDGE,"E745"),sQuery(id+"F2.wireOp",EDGE,"E746"),sQuery(id+"F2.wireOp",EDGE,"E747"),sQuery(id+"F2.wireOp",EDGE,"E748"),sQuery(id+"F2.wireOp",EDGE,"E749"),sQuery(id+"F2.wireOp",EDGE,"E750"),sQuery(id+"F2.wireOp",EDGE,"E751"),sQuery(id+"F2.wireOp",EDGE,"E752"),sQuery(id+"F2.wireOp",EDGE,"E753"),sQuery(id+"F2.wireOp",EDGE,"E754"),sQuery(id+"F2.wireOp",EDGE,"E755"),sQuery(id+"F2.wireOp",EDGE,"E756"),sQuery(id+"F2.wireOp",EDGE,"E757"),sQuery(id+"F2.wireOp",EDGE,"E758"),sQuery(id+"F2.wireOp",EDGE,"E759"),sQuery(id+"F2.wireOp",EDGE,"E760"),sQuery(id+"F2.wireOp",EDGE,"E761"),sQuery(id+"F2.wireOp",EDGE,"E762"),sQuery(id+"F2.wireOp",EDGE,"E763"),sQuery(id+"F2.wireOp",EDGE,"E764"),sQuery(id+"F2.wireOp",EDGE,"E765"),sQuery(id+"F2.wireOp",EDGE,"E766"),sQuery(id+"F2.wireOp",EDGE,"E767"),sQuery(id+"F2.wireOp",EDGE,"E768"),sQuery(id+"F2.wireOp",EDGE,"E769"),sQuery(id+"F2.wireOp",EDGE,"E770"),sQuery(id+"F2.wireOp",EDGE,"E771"),sQuery(id+"F2.wireOp",EDGE,"E772"),sQuery(id+"F2.wireOp",EDGE,"E773"),sQuery(id+"F2.wireOp",EDGE,"E774"),sQuery(id+"F2.wireOp",EDGE,"E775"),sQuery(id+"F2.wireOp",EDGE,"E776"),sQuery(id+"F2.wireOp",EDGE,"E777"),sQuery(id+"F2.wireOp",EDGE,"E778"),sQuery(id+"F2.wireOp",EDGE,"E779"),sQuery(id+"F2.wireOp",EDGE,"E780"),sQuery(id+"F2.wireOp",EDGE,"E781"),sQuery(id+"F2.wireOp",EDGE,"E782"),sQuery(id+"F2.wireOp",EDGE,"E783"),sQuery(id+"F2.wireOp",EDGE,"E784"),sQuery(id+"F2.wireOp",EDGE,"E785"),sQuery(id+"F2.wireOp",EDGE,"E786"),sQuery(id+"F2.wireOp",EDGE,"E787"),sQuery(id+"F2.wireOp",EDGE,"E788"),sQuery(id+"F2.wireOp",EDGE,"E789"),sQuery(id+"F2.wireOp",EDGE,"E790"),sQuery(id+"F2.wireOp",EDGE,"E791"),sQuery(id+"F2.wireOp",EDGE,"E792"),sQuery(id+"F2.wireOp",EDGE,"E793"),sQuery(id+"F2.wireOp",EDGE,"E794"),sQuery(id+"F2.wireOp",EDGE,"E795"),sQuery(id+"F2.wireOp",EDGE,"E796"),sQuery(id+"F2.wireOp",EDGE,"E797"),sQuery(id+"F2.wireOp",EDGE,"E798"),sQuery(id+"F2.wireOp",EDGE,"E799"),sQuery(id+"F2.wireOp",EDGE,"E800"),sQuery(id+"F2.wireOp",EDGE,"E801"),sQuery(id+"F2.wireOp",EDGE,"E802"),sQuery(id+"F2.wireOp",EDGE,"E803"),sQuery(id+"F2.wireOp",EDGE,"E804"),sQuery(id+"F2.wireOp",EDGE,"E805"),sQuery(id+"F2.wireOp",EDGE,"E806"),sQuery(id+"F2.wireOp",EDGE,"E807"),sQuery(id+"F2.wireOp",EDGE,"E808"),sQuery(id+"F2.wireOp",EDGE,"E809"),sQuery(id+"F2.wireOp",EDGE,"E810"),sQuery(id+"F2.wireOp",EDGE,"E811"),sQuery(id+"F2.wireOp",EDGE,"E812"),sQuery(id+"F2.wireOp",EDGE,"E813"),sQuery(id+"F2.wireOp",EDGE,"E814"),sQuery(id+"F2.wireOp",EDGE,"E815"),sQuery(id+"F2.wireOp",EDGE,"E816"),sQuery(id+"F2.wireOp",EDGE,"E817"),sQuery(id+"F2.wireOp",EDGE,"E818"),sQuery(id+"F2.wireOp",EDGE,"E819"),sQuery(id+"F2.wireOp",EDGE,"E820"),sQuery(id+"F2.wireOp",EDGE,"E821"),sQuery(id+"F2.wireOp",EDGE,"E822"),sQuery(id+"F2.wireOp",EDGE,"E823"),sQuery(id+"F2.wireOp",EDGE,"E824"),sQuery(id+"F2.wireOp",EDGE,"E825"),sQuery(id+"F2.wireOp",EDGE,"E826"),sQuery(id+"F2.wireOp",EDGE,"E827"),sQuery(id+"F2.wireOp",EDGE,"E828"),sQuery(id+"F2.wireOp",EDGE,"E829"),sQuery(id+"F2.wireOp",EDGE,"E830"),sQuery(id+"F2.wireOp",EDGE,"E831"),sQuery(id+"F2.wireOp",EDGE,"E832"),sQuery(id+"F2.wireOp",EDGE,"E833"),sQuery(id+"F2.wireOp",EDGE,"E834"),sQuery(id+"F2.wireOp",EDGE,"E835"),sQuery(id+"F2.wireOp",EDGE,"E836"),sQuery(id+"F2.wireOp",EDGE,"E837"),sQuery(id+"F2.wireOp",EDGE,"E838"),sQuery(id+"F2.wireOp",EDGE,"E839"),sQuery(id+"F2.wireOp",EDGE,"E840"),sQuery(id+"F2.wireOp",EDGE,"E841"),sQuery(id+"F2.wireOp",EDGE,"E842"),sQuery(id+"F2.wireOp",EDGE,"E843"),sQuery(id+"F2.wireOp",EDGE,"E844"),sQuery(id+"F2.wireOp",EDGE,"E845"),sQuery(id+"F2.wireOp",EDGE,"E846"),sQuery(id+"F2.wireOp",EDGE,"E847"),sQuery(id+"F2.wireOp",EDGE,"E848"),sQuery(id+"F2.wireOp",EDGE,"E849"),sQuery(id+"F2.wireOp",EDGE,"E850"),sQuery(id+"F2.wireOp",EDGE,"E851"),sQuery(id+"F2.wireOp",EDGE,"E852"),sQuery(id+"F2.wireOp",EDGE,"E853"),sQuery(id+"F2.wireOp",EDGE,"E854"),sQuery(id+"F2.wireOp",EDGE,"E855"),sQuery(id+"F2.wireOp",EDGE,"E856"),sQuery(id+"F2.wireOp",EDGE,"E857"),sQuery(id+"F2.wireOp",EDGE,"E858"),sQuery(id+"F2.wireOp",EDGE,"E859"),sQuery(id+"F2.wireOp",EDGE,"E860"),sQuery(id+"F2.wireOp",EDGE,"E861"),sQuery(id+"F2.wireOp",EDGE,"E862"),sQuery(id+"F2.wireOp",EDGE,"E863"),sQuery(id+"F2.wireOp",EDGE,"E864"),sQuery(id+"F2.wireOp",EDGE,"E865"),sQuery(id+"F2.wireOp",EDGE,"E866"),sQuery(id+"F2.wireOp",EDGE,"E867"),sQuery(id+"F2.wireOp",EDGE,"E868"),sQuery(id+"F2.wireOp",EDGE,"E869"),sQuery(id+"F2.wireOp",EDGE,"E870"),sQuery(id+"F2.wireOp",EDGE,"E871"),sQuery(id+"F2.wireOp",EDGE,"E872"),sQuery(id+"F2.wireOp",EDGE,"E873"),sQuery(id+"F2.wireOp",EDGE,"E874"),sQuery(id+"F2.wireOp",EDGE,"E875"),sQuery(id+"F2.wireOp",EDGE,"E876"),sQuery(id+"F2.wireOp",EDGE,"E877"),sQuery(id+"F2.wireOp",EDGE,"E878"),sQuery(id+"F2.wireOp",EDGE,"E879"),sQuery(id+"F2.wireOp",EDGE,"E880"),sQuery(id+"F2.wireOp",EDGE,"E881"),sQuery(id+"F2.wireOp",EDGE,"E882"),sQuery(id+"F2.wireOp",EDGE,"E883"),sQuery(id+"F2.wireOp",EDGE,"E884"),sQuery(id+"F2.wireOp",EDGE,"E885"),sQuery(id+"F2.wireOp",EDGE,"E886"),sQuery(id+"F2.wireOp",EDGE,"E887"),sQuery(id+"F2.wireOp",EDGE,"E888"),sQuery(id+"F2.wireOp",EDGE,"E889"),sQuery(id+"F2.wireOp",EDGE,"E890"),sQuery(id+"F2.wireOp",EDGE,"E891"),sQuery(id+"F2.wireOp",EDGE,"E892"),sQuery(id+"F2.wireOp",EDGE,"E893"),sQuery(id+"F2.wireOp",EDGE,"E894"),sQuery(id+"F2.wireOp",EDGE,"E895"),sQuery(id+"F2.wireOp",EDGE,"E896"),sQuery(id+"F2.wireOp",EDGE,"E897"),sQuery(id+"F2.wireOp",EDGE,"E898"),sQuery(id+"F2.wireOp",EDGE,"E899"),sQuery(id+"F2.wireOp",EDGE,"E900"),sQuery(id+"F2.wireOp",EDGE,"E901"),sQuery(id+"F2.wireOp",EDGE,"E902"),sQuery(id+"F2.wireOp",EDGE,"E903"),sQuery(id+"F2.wireOp",EDGE,"E904"),sQuery(id+"F2.wireOp",EDGE,"E905"),sQuery(id+"F2.wireOp",EDGE,"E906"),sQuery(id+"F2.wireOp",EDGE,"E907"),sQuery(id+"F2.wireOp",EDGE,"E908"),sQuery(id+"F2.wireOp",EDGE,"E909"),sQuery(id+"F2.wireOp",EDGE,"E910"),sQuery(id+"F2.wireOp",EDGE,"E911"),sQuery(id+"F2.wireOp",EDGE,"E912"),sQuery(id+"F2.wireOp",EDGE,"E913"),sQuery(id+"F2.wireOp",EDGE,"E914"),sQuery(id+"F2.wireOp",EDGE,"E915"),sQuery(id+"F2.wireOp",EDGE,"E916"),sQuery(id+"F2.wireOp",EDGE,"E917"),sQuery(id+"F2.wireOp",EDGE,"E918")])],"isStart":true});
            extrude(context, id + "F6", {"entities" : qUnion([Q0]), "operationType" : NewBodyOperationType.ADD, "depth" : 2.54 * mm});
        }
    });
